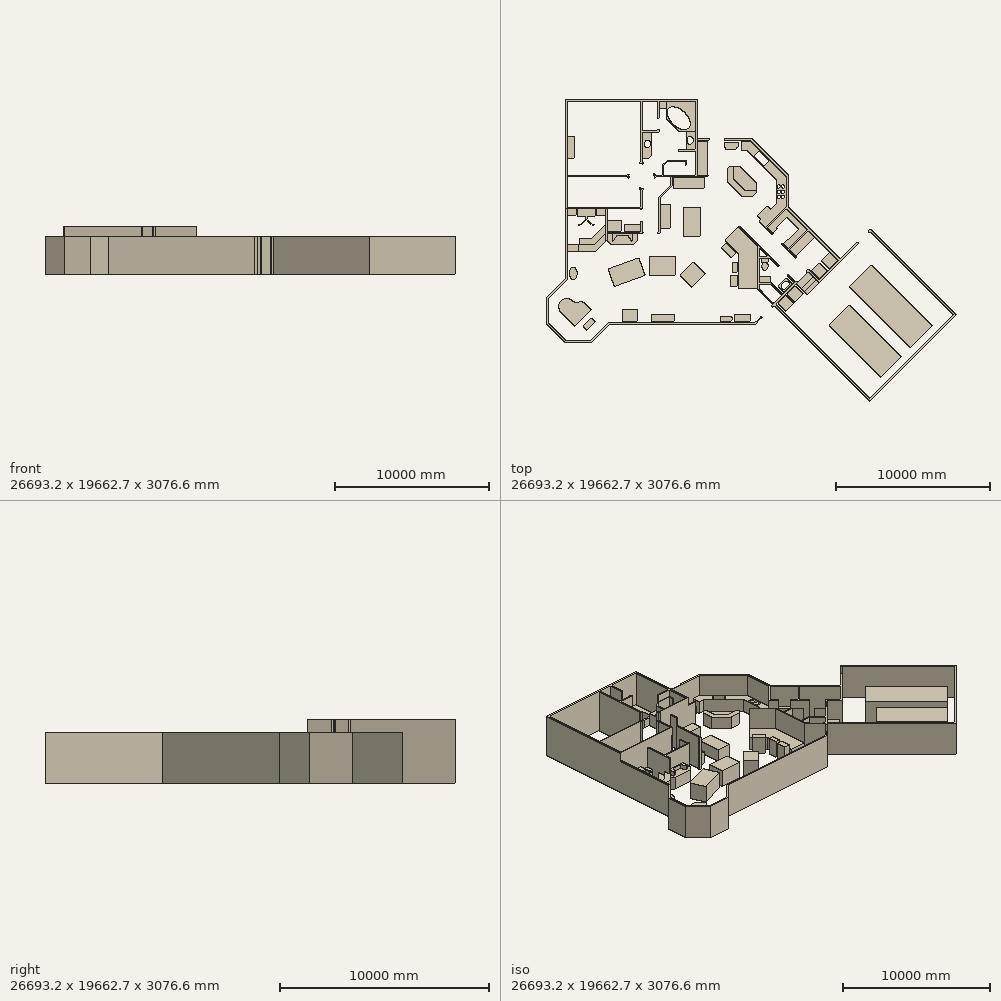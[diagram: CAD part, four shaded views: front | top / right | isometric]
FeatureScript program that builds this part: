
annotation { "Feature Type Name" : "Feature", "Feature Type Description" : "" }
export const myFeature = defineFeature(function(context is Context, id is Id, definition is map)
    precondition{}
    {
        {
            var Q0;
            Q0=qCreatedBy(makeId("Top.planeOp"),FACE);
            var sketch = newSketch(context, id + "F0", { "sketchPlane" : qUnion([Q0])});
            skEllipse(sketch, "E0", {"center": v(0, 0) * mm, "majorRadius": 914.4 * mm, "minorRadius": 533.4 * mm, "majorAxis": v(0.7, -0.7)});
            skLineSegment(sketch, "E1", {"start": v(-646.58, 646.58) * mm, "end": v(646.58, -646.58) * mm, "construction": true});
            skLineSegment(sketch, "E2", {"start": v(377.17, 377.17) * mm, "end": v(-377.17, -377.17) * mm, "construction": true});
            skLineSegment(sketch, "E3", {"start": v(-1281.95, 1090.6) * mm, "end": v(94.8, 1090.6) * mm});
            skLineSegment(sketch, "E4", {"start": v(94.8, 1090.6) * mm, "end": v(1090.6, 94.8) * mm, "construction": true});
            skLineSegment(sketch, "E5", {"start": v(1090.6, 94.8) * mm, "end": v(1090.6, -2043.95) * mm});
            skLineSegment(sketch, "E6", {"start": v(748.55, -368.46) * mm, "end": v(1090.6, -368.46) * mm, "construction": true});
            skLineSegment(sketch, "E7", {"start": v(-368.46, 748.55) * mm, "end": v(-368.46, 1090.6) * mm, "construction": true});
            skLineSegment(sketch, "E8", {"start": v(-368.46, 748.55) * mm, "end": v(436.85, 748.55) * mm, "construction": true});
            skLineSegment(sketch, "E9", {"start": v(748.55, -368.46) * mm, "end": v(748.55, 436.85) * mm, "construction": true});
            skLineSegment(sketch, "E10", {"start": v(377.17, 377.17) * mm, "end": v(592.7, 592.7) * mm, "construction": true});
            skLineSegment(sketch, "E11", {"start": v(-824.75, 1090.6) * mm, "end": v(-824.75, -37.36) * mm});
            skLineSegment(sketch, "E12", {"start": v(-824.75, -37.36) * mm, "end": v(-37.36, -824.75) * mm});
            skLineSegment(sketch, "E13", {"start": v(-37.36, -824.75) * mm, "end": v(1090.6, -824.75) * mm});
            skLineSegment(sketch, "E14", {"start": v(-377.17, -377.17) * mm, "end": v(-431.05, -431.05) * mm, "construction": true});
            skLineSegment(sketch, "E15", {"start": v(368.46, -824.75) * mm, "end": v(368.46, -748.55) * mm, "construction": true});
            skLineSegment(sketch, "E16", {"start": v(368.46, -748.55) * mm, "end": v(1090.6, -748.55) * mm, "construction": true});
            skLineSegment(sketch, "E17", {"start": v(-824.75, 368.46) * mm, "end": v(-748.55, 368.46) * mm, "construction": true});
            skLineSegment(sketch, "E18", {"start": v(-748.55, 368.46) * mm, "end": v(-748.55, 1090.6) * mm, "construction": true});
            skLineSegment(sketch, "E19", {"start": v(-1281.95, 1090.6) * mm, "end": v(-1281.95, 17.6) * mm});
            skLineSegment(sketch, "E20", {"start": v(-1281.95, 17.6) * mm, "end": v(-1370.85, 17.6) * mm});
            skLineSegment(sketch, "E21", {"start": v(-1370.85, 17.6) * mm, "end": v(-1370.85, 1090.6) * mm});
            skLineSegment(sketch, "E22", {"start": v(-1370.85, 1090.6) * mm, "end": v(-2386.85, 1090.6) * mm});
            skLineSegment(sketch, "E23", {"start": v(-2386.85, 1090.6) * mm, "end": v(-2386.85, -820.6) * mm});
            skLineSegment(sketch, "E24", {"start": v(-2386.85, -820.6) * mm, "end": v(-1370.85, -820.6) * mm});
            skLineSegment(sketch, "E25", {"start": v(-1281.95, -909.5) * mm, "end": v(-2386.85, -909.5) * mm});
            skLineSegment(sketch, "E26", {"start": v(-1370.85, -820.6) * mm, "end": v(-1281.95, -820.6) * mm, "construction": true});
            skLineSegment(sketch, "E27", {"start": v(-1777.25, -909.5) * mm, "end": v(-1777.25, -2433.5) * mm});
            skEllipse(sketch, "E28", {"center": v(-2031.25, -1671.5) * mm, "majorRadius": 254 * mm, "minorRadius": 203.2 * mm, "majorAxis": v(0, -1)});
            skLineSegment(sketch, "E29", {"start": v(-2031.25, -1417.5) * mm, "end": v(-2031.25, -1925.5) * mm, "construction": true});
            skLineSegment(sketch, "E30", {"start": v(-2234.45, -1671.5) * mm, "end": v(-1828.05, -1671.5) * mm, "construction": true});
            skLineSegment(sketch, "E31", {"start": v(-1828.05, -1671.5) * mm, "end": v(-1777.25, -1671.5) * mm, "construction": true});
            skLineSegment(sketch, "E32", {"start": v(-1320.05, -820.6) * mm, "end": v(-1320.05, -909.5) * mm, "construction": true});
            skLineSegment(sketch, "E33", {"start": v(-1358.15, -820.6) * mm, "end": v(-1358.15, -909.5) * mm, "construction": true});
            skLineSegment(sketch, "E34", {"start": v(-1396.25, -820.6) * mm, "end": v(-1396.25, -909.5) * mm, "construction": true});
            skLineSegment(sketch, "E35", {"start": v(-1358.15, -858.7) * mm, "end": v(-1320.05, -858.7) * mm, "construction": true});
            skLineSegment(sketch, "E36", {"start": v(-1764.55, -820.6) * mm, "end": v(-1764.55, -909.5) * mm, "construction": true});
            skLineSegment(sketch, "E37", {"start": v(-1802.65, -909.5) * mm, "end": v(-1802.65, -820.6) * mm, "construction": true});
            skLineSegment(sketch, "E38", {"start": v(-1281.95, 633.4) * mm, "end": v(-824.75, 633.4) * mm});
            skLineSegment(sketch, "E39", {"start": v(-1370.85, 1052.5) * mm, "end": v(-1281.95, 1052.5) * mm, "construction": true});
            skLineSegment(sketch, "E40", {"start": v(-1370.85, 1014.4) * mm, "end": v(-1281.95, 1014.4) * mm, "construction": true});
            skLineSegment(sketch, "E41", {"start": v(-1370.85, 1090.6) * mm, "end": v(-1281.95, 1090.6) * mm, "construction": true});
            skLineSegment(sketch, "E42", {"start": v(-2386.85, -909.5) * mm, "end": v(-2386.85, -2827.58) * mm});
            skLineSegment(sketch, "E43", {"start": v(-2386.85, -2827.58) * mm, "end": v(-2279.08, -2935.34) * mm});
            skLineSegment(sketch, "E44", {"start": v(-2279.08, -2935.34) * mm, "end": v(-2341.94, -2998.2) * mm});
            skLineSegment(sketch, "E45", {"start": v(-2341.94, -2998.2) * mm, "end": v(-2449.7, -2890.44) * mm});
            skLineSegment(sketch, "E46", {"start": v(1090.6, -3707.65) * mm, "end": v(-986.98, -3707.65) * mm});
            skLineSegment(sketch, "E47", {"start": v(-1506.78, -3707.65) * mm, "end": v(-1614.54, -3599.88) * mm});
            skLineSegment(sketch, "E48", {"start": v(-1614.54, -3599.88) * mm, "end": v(-1677.4, -3662.74) * mm});
            skLineSegment(sketch, "E49", {"start": v(-1677.4, -3662.74) * mm, "end": v(-1569.64, -3770.5) * mm});
            skLineSegment(sketch, "E50", {"start": v(-1469.96, -3796.55) * mm, "end": v(1230.3, -3796.55) * mm});
            skLineSegment(sketch, "E51", {"start": v(-1777.25, -2433.5) * mm, "end": v(-1929.65, -2585.9) * mm});
            skLineSegment(sketch, "E52", {"start": v(-2386.85, -2585.9) * mm, "end": v(-1929.65, -2585.9) * mm});
            skLineSegment(sketch, "E53", {"start": v(481, -824.75) * mm, "end": v(481, -2043.95) * mm});
            skLineSegment(sketch, "E54", {"start": v(1090.6, -2043.95) * mm, "end": v(-14.3, -2043.95) * mm});
            skLineSegment(sketch, "E55", {"start": v(-14.3, -2043.95) * mm, "end": v(-14.3, -2132.85) * mm});
            skLineSegment(sketch, "E56", {"start": v(-14.3, -2132.85) * mm, "end": v(1090.6, -2132.85) * mm});
            skLineSegment(sketch, "E57.trimOffspring", {"start": v(1090.6, -2132.85) * mm, "end": v(1090.6, -3707.65) * mm});
            skLineSegment(sketch, "E58", {"start": v(-1075.88, -3707.65) * mm, "end": v(-1075.88, -3061.22) * mm});
            skLineSegment(sketch, "E59", {"start": v(-1075.88, -3061.22) * mm, "end": v(-942.08, -2927.42) * mm});
            skLineSegment(sketch, "E60", {"start": v(-942.08, -2927.42) * mm, "end": v(-915.14, -2954.36) * mm});
            skLineSegment(sketch, "E61", {"start": v(-915.14, -2954.36) * mm, "end": v(-703.23, -2742.45) * mm});
            skLineSegment(sketch, "E62", {"start": v(-703.23, -2742.45) * mm, "end": v(481, -2742.45) * mm});
            skLineSegment(sketch, "E63", {"start": v(481, -2742.45) * mm, "end": v(481, -3098.05) * mm});
            skLineSegment(sketch, "E64", {"start": v(481, -3098.05) * mm, "end": v(430.2, -3098.05) * mm});
            skLineSegment(sketch, "E65", {"start": v(430.2, -3098.05) * mm, "end": v(430.2, -2793.25) * mm});
            skLineSegment(sketch, "E66", {"start": v(430.2, -2793.25) * mm, "end": v(-682.18, -2793.25) * mm});
            skLineSegment(sketch, "E67", {"start": v(-682.18, -2793.25) * mm, "end": v(-986.98, -3098.05) * mm});
            skLineSegment(sketch, "E68", {"start": v(-986.98, -3098.05) * mm, "end": v(-986.98, -3707.65) * mm});
            skLineSegment(sketch, "E69.trimOffspring", {"start": v(-1075.88, -3707.65) * mm, "end": v(-1506.78, -3707.65) * mm});
            skLineSegment(sketch, "E70", {"start": v(-1506.78, -3707.65) * mm, "end": v(-1075.88, -3276.75) * mm, "construction": true});
            skLineSegment(sketch, "E71", {"start": v(531.8, -1434.35) * mm, "end": v(938.2, -1434.35) * mm, "construction": true});
            skLineSegment(sketch, "E72", {"start": v(531.8, -1434.35) * mm, "end": v(481, -1434.35) * mm, "construction": true});
            skEllipse(sketch, "E73", {"center": v(735, -1434.35) * mm, "majorRadius": 254 * mm, "minorRadius": 203.2 * mm, "majorAxis": v(0, 1)});
            skLineSegment(sketch, "E74", {"start": v(-2475.75, -2790.76) * mm, "end": v(-2475.75, 1090.6) * mm});
            skLineSegment(sketch, "E75", {"start": v(-2475.75, 1090.6) * mm, "end": v(-6278.2, 1090.6) * mm});
            skLineSegment(sketch, "E76", {"start": v(-6278.2, 1090.6) * mm, "end": v(-7273.99, 94.8) * mm, "construction": true});
            skLineSegment(sketch, "E77", {"start": v(-7273.99, 94.8) * mm, "end": v(-7273.99, -3707.65) * mm});
            skLineSegment(sketch, "E78", {"start": v(-1569.64, -3770.5) * mm, "end": v(-1623.52, -3824.39) * mm});
            skLineSegment(sketch, "E79", {"start": v(-1560.66, -3887.25) * mm, "end": v(-1469.96, -3796.55) * mm});
            skLineSegment(sketch, "E80", {"start": v(-1623.52, -3824.39) * mm, "end": v(-1560.66, -3887.25) * mm});
            skLineSegment(sketch, "E81", {"start": v(-2475.75, -5777.75) * mm, "end": v(-2475.75, -4676.61) * mm});
            skLineSegment(sketch, "E82", {"start": v(-2475.75, -4676.61) * mm, "end": v(-2583.5, -4568.85) * mm});
            skLineSegment(sketch, "E83", {"start": v(-2583.5, -4568.85) * mm, "end": v(-2520.65, -4505.99) * mm});
            skLineSegment(sketch, "E84", {"start": v(-2520.65, -4505.99) * mm, "end": v(-2412.88, -4613.75) * mm});
            skLineSegment(sketch, "E85", {"start": v(-2412.88, -4613.75) * mm, "end": v(-2359, -4559.87) * mm});
            skLineSegment(sketch, "E86", {"start": v(-2359, -4559.87) * mm, "end": v(-2296.14, -4622.73) * mm});
            skLineSegment(sketch, "E87", {"start": v(-2296.14, -4622.73) * mm, "end": v(-2386.85, -4713.43) * mm});
            skLineSegment(sketch, "E88", {"start": v(-2386.85, -4713.43) * mm, "end": v(-2386.85, -5866.65) * mm});
            skLineSegment(sketch, "E89", {"start": v(-7273.99, -3707.65) * mm, "end": v(-3392.63, -3707.65) * mm});
            skLineSegment(sketch, "E90", {"start": v(-3292.95, -3733.68) * mm, "end": v(-3185.19, -3841.45) * mm});
            skLineSegment(sketch, "E91", {"start": v(-3185.19, -3841.45) * mm, "end": v(-3248.05, -3904.3) * mm});
            skLineSegment(sketch, "E92", {"start": v(-3248.05, -3904.3) * mm, "end": v(-3355.81, -3796.55) * mm});
            skLineSegment(sketch, "E93", {"start": v(-3355.81, -3796.55) * mm, "end": v(-7273.99, -3796.55) * mm});
            skLineSegment(sketch, "E94", {"start": v(-3292.95, -3733.68) * mm, "end": v(-3239.07, -3679.8) * mm});
            skLineSegment(sketch, "E95", {"start": v(-3392.63, -3707.65) * mm, "end": v(-3301.93, -3616.94) * mm});
            skLineSegment(sketch, "E96", {"start": v(-3301.93, -3616.94) * mm, "end": v(-3239.07, -3679.8) * mm});
            skLineSegment(sketch, "E97", {"start": v(-2566.45, -2881.46) * mm, "end": v(-2503.59, -2944.32) * mm});
            skLineSegment(sketch, "E98.trimOffspring", {"start": v(-2566.45, -2881.46) * mm, "end": v(-2475.75, -2790.76) * mm});
            skLineSegment(sketch, "E99.trimOffspring", {"start": v(-2503.59, -2944.32) * mm, "end": v(-2449.7, -2890.44) * mm});
            skLineSegment(sketch, "E100", {"start": v(-7273.99, -3796.55) * mm, "end": v(-7273.99, -5777.75) * mm});
            skLineSegment(sketch, "E101", {"start": v(-7273.99, -5777.75) * mm, "end": v(-2475.75, -5777.75) * mm});
            skLineSegment(sketch, "E102.0", {"start": v(-7413.69, 152.66) * mm, "end": v(-7413.69, -5866.65) * mm});
            skLineSegment(sketch, "E102.1", {"start": v(-6336.06, 1230.3) * mm, "end": v(-7413.69, 152.66) * mm, "construction": true});
            skLineSegment(sketch, "E102.2", {"start": v(152.66, 1230.3) * mm, "end": v(-6336.06, 1230.3) * mm});
            skLineSegment(sketch, "E103.0", {"start": v(1230.3, 152.66) * mm, "end": v(1230.3, -3796.55) * mm});
            skLineSegment(sketch, "E104.0", {"start": v(152.66, 1230.3) * mm, "end": v(1230.3, 152.66) * mm, "construction": true});
            skLineSegment(sketch, "E105", {"start": v(-3355.81, -3796.55) * mm, "end": v(-3965.41, -4406.15) * mm, "construction": true});
            skLineSegment(sketch, "E106", {"start": v(-7273.99, -4406.15) * mm, "end": v(-3965.41, -4406.15) * mm, "construction": true});
            skLineSegment(sketch, "E107", {"start": v(-7273.99, -5168.15) * mm, "end": v(-2475.75, -5168.15) * mm, "construction": true});
            skLineSegment(sketch, "E108", {"start": v(-6867.59, -4406.15) * mm, "end": v(-6867.59, -5168.15) * mm, "construction": true});
            skLineSegment(sketch, "E109", {"start": v(-7413.69, -5866.65) * mm, "end": v(-2386.85, -5866.65) * mm});
            skLineSegment(sketch, "E110.bottom", {"start": v(-3034.55, 1090.6) * mm, "end": v(-2475.75, 1090.6) * mm});
            skLineSegment(sketch, "E110.top", {"start": v(-3034.55, 608) * mm, "end": v(-2475.75, 608) * mm});
            skLineSegment(sketch, "E110.left", {"start": v(-3034.55, 1090.6) * mm, "end": v(-3034.55, 608) * mm});
            skLineSegment(sketch, "E110.right", {"start": v(-2475.75, 1090.6) * mm, "end": v(-2475.75, 608) * mm});
            skLineSegment(sketch, "E111.bottom", {"start": v(-3110.75, 1090.6) * mm, "end": v(-4787.15, 1090.6) * mm});
            skLineSegment(sketch, "E111.top", {"start": v(-3110.75, -1347.8) * mm, "end": v(-4787.15, -1347.8) * mm});
            skLineSegment(sketch, "E111.left", {"start": v(-3110.75, 1090.6) * mm, "end": v(-3110.75, -1347.8) * mm});
            skLineSegment(sketch, "E111.right", {"start": v(-4787.15, 1090.6) * mm, "end": v(-4787.15, -1347.8) * mm});
            skLineSegment(sketch, "E112.bottom", {"start": v(-4863.35, 1090.6) * mm, "end": v(-5422.15, 1090.6) * mm});
            skLineSegment(sketch, "E112.top", {"start": v(-4863.35, 608) * mm, "end": v(-5422.15, 608) * mm});
            skLineSegment(sketch, "E112.left", {"start": v(-4863.35, 1090.6) * mm, "end": v(-4863.35, 608) * mm});
            skLineSegment(sketch, "E112.right", {"start": v(-5422.15, 1090.6) * mm, "end": v(-5422.15, 608) * mm});
            skLineSegment(sketch, "E113.trimOffspring", {"start": v(-1281.95, -820.6) * mm, "end": v(-1281.95, -909.5) * mm});
            skLineSegment(sketch, "E114", {"start": v(-1370.85, -820.6) * mm, "end": v(-1370.85, -744.4) * mm});
            skLineSegment(sketch, "E115", {"start": v(-1370.85, -744.4) * mm, "end": v(-1281.95, -744.4) * mm});
            skLineSegment(sketch, "E116", {"start": v(-1281.95, -744.4) * mm, "end": v(-1281.95, -820.6) * mm});
            skLineSegment(sketch, "E117", {"start": v(-1281.95, -820.6) * mm, "end": v(-1281.95, -820.6) * mm});
            skLineSegment(sketch, "E118.bottom", {"start": v(-7273.99, -1167.65) * mm, "end": v(-6791.39, -1167.65) * mm});
            skLineSegment(sketch, "E118.top", {"start": v(-7273.99, -2640.85) * mm, "end": v(-6791.39, -2640.85) * mm});
            skLineSegment(sketch, "E118.left", {"start": v(-7273.99, -1167.65) * mm, "end": v(-7273.99, -2640.85) * mm});
            skLineSegment(sketch, "E118.right", {"start": v(-6791.39, -1167.65) * mm, "end": v(-6791.39, -2640.85) * mm});
            skLineSegment(sketch, "E119.bottom", {"start": v(-7273.99, -3707.65) * mm, "end": v(-6918.39, -3707.65) * mm});
            skLineSegment(sketch, "E119.top", {"start": v(-7273.99, -2945.65) * mm, "end": v(-6918.39, -2945.65) * mm});
            skLineSegment(sketch, "E119.left", {"start": v(-7273.99, -3707.65) * mm, "end": v(-7273.99, -2945.65) * mm});
            skLineSegment(sketch, "E119.right", {"start": v(-6918.39, -3707.65) * mm, "end": v(-6918.39, -2945.65) * mm});
            skLineSegment(sketch, "E120", {"start": v(94.8, 1090.6) * mm, "end": v(1090.6, 1090.6) * mm});
            skLineSegment(sketch, "E121", {"start": v(152.66, 1230.3) * mm, "end": v(1230.3, 1230.3) * mm});
            skLineSegment(sketch, "E122", {"start": v(1090.6, 94.8) * mm, "end": v(1090.6, 1090.6) * mm});
            skLineSegment(sketch, "E123", {"start": v(1230.3, 152.66) * mm, "end": v(1230.3, 1230.3) * mm});
            skLineSegment(sketch, "E124", {"start": v(-6336.06, 1230.3) * mm, "end": v(-7413.69, 1230.3) * mm});
            skLineSegment(sketch, "E125", {"start": v(-6278.2, 1090.6) * mm, "end": v(-7273.99, 1090.6) * mm});
            skLineSegment(sketch, "E126", {"start": v(-7413.69, 152.66) * mm, "end": v(-7413.69, 1230.3) * mm});
            skLineSegment(sketch, "E127", {"start": v(-7273.99, 94.8) * mm, "end": v(-7273.99, 1090.6) * mm});
            skSolve(sketch);
        }
        {
            var Q0;
            {var subQ13=sQuery(id+"F0.wireOp",EDGE,"E20");Q0=makeQuery(id+"F0.imprint","IMPRINT",FACE,{"disambiguationData":[TD([[makeQuery(id+"F0.imprint","IMPRINT",EDGE,{"derivedFrom":subQ13}),-1.0]])]});}
            extrude(context, id + "F1", {"entities" : qUnion([Q0]), "depth" : 3076.57 * mm, "offsetDistance" : 25.4 * mm});
        }
        {
            var Q0;
            {var subQ3=sQuery(id+"F0.wireOp",EDGE,"E53");Q0=makeQuery(id+"F0.imprint","IMPRINT",FACE,{"disambiguationData":[TD([[makeQuery(id+"F0.imprint","IMPRINT",EDGE,{"derivedFrom":subQ3}),1.0]])]});}
            var Q1;
            {var subQ4=sQuery(id+"F0.wireOp",EDGE,"E27");Q1=makeQuery(id+"F0.imprint","IMPRINT",FACE,{"disambiguationData":[TD([[makeQuery(id+"F0.imprint","IMPRINT",EDGE,{"derivedFrom":subQ4}),-1.0]])]});}
            var Q2;
            Q2=makeQuery(id+"F0.imprint","IMPRINT",FACE,{"disambiguationData":[TD([[makeQuery(id+"F0.imprint","IMPRINT",EDGE,{"derivedFrom":sQuery(id+"F0.wireOp",EDGE,"E112.bottom")}),1.0]])]});
            var Q3;
            Q3=makeQuery(id+"F0.imprint","IMPRINT",FACE,{"disambiguationData":[TD([[makeQuery(id+"F0.imprint","IMPRINT",EDGE,{"derivedFrom":sQuery(id+"F0.wireOp",EDGE,"E111.bottom")}),1.0]])]});
            var Q4;
            Q4=makeQuery(id+"F0.imprint","IMPRINT",FACE,{"disambiguationData":[TD([[makeQuery(id+"F0.imprint","IMPRINT",EDGE,{"derivedFrom":sQuery(id+"F0.wireOp",EDGE,"E110.bottom")}),-1.0]])]});
            var Q5;
            Q5=makeQuery(id+"F0.imprint","IMPRINT",FACE,{"disambiguationData":[TD([[makeQuery(id+"F0.imprint","IMPRINT",EDGE,{"derivedFrom":sQuery(id+"F0.wireOp",EDGE,"E118.bottom")}),-1.0]])]});
            var Q6;
            Q6=makeQuery(id+"F0.imprint","IMPRINT",FACE,{"disambiguationData":[TD([[makeQuery(id+"F0.imprint","IMPRINT",EDGE,{"derivedFrom":sQuery(id+"F0.wireOp",EDGE,"E119.bottom")}),1.0]])]});
            var Q7;
            {var subQ5=sQuery(id+"F0.wireOp",EDGE,"E38");Q7=makeQuery(id+"F0.imprint","IMPRINT",FACE,{"disambiguationData":[TD([[makeQuery(id+"F0.imprint","IMPRINT",EDGE,{"derivedFrom":subQ5}),1.0]])]});}
            extrude(context, id + "F2", {"entities" : qUnion([Q0, Q1, Q2, Q3, Q4, Q5, Q6, Q7]), "depth" : 914.4 * mm, "offsetDistance" : 25.4 * mm});
        }
        {
            var Q0;
            Q0=makeQuery(id+"F0.imprint","IMPRINT",FACE,{"disambiguationData":[TD([[makeQuery(id+"F0.imprint","IMPRINT",EDGE,{"derivedFrom":sQuery(id+"F0.wireOp",EDGE,"E0")}),-1.0]])]});
            extrude(context, id + "F3", {"entities" : qUnion([Q0]), "depth" : 609.6 * mm, "offsetDistance" : 25.4 * mm});
        }
        {
            var Q0;
            Q0=qCreatedBy(makeId("Top.planeOp"),FACE);
            var sketch = newSketch(context, id + "F4", { "sketchPlane" : qUnion([Q0])});
            skLineSegment(sketch, "E128", {"start": v(-7413.69, -5866.65) * mm, "end": v(-7413.69, -10507.78) * mm});
            skLineSegment(sketch, "E129", {"start": v(-7413.69, -10507.78) * mm, "end": v(-8618.88, -11712.98) * mm});
            skLineSegment(sketch, "E130", {"start": v(-8618.88, -11712.98) * mm, "end": v(-8618.88, -13417.38) * mm});
            skLineSegment(sketch, "E131", {"start": v(-8618.88, -13417.38) * mm, "end": v(-7413.69, -14622.58) * mm});
            skLineSegment(sketch, "E132", {"start": v(-7413.69, -14622.58) * mm, "end": v(-5709.28, -14622.58) * mm});
            skLineSegment(sketch, "E133", {"start": v(-5709.28, -14622.58) * mm, "end": v(-4504.08, -13417.38) * mm});
            skLineSegment(sketch, "E134", {"start": v(-4504.08, -13417.38) * mm, "end": v(5003.07, -13417.38) * mm});
            skLineSegment(sketch, "E135", {"start": v(-7413.69, -5866.65) * mm, "end": v(-7273.99, -5866.65) * mm});
            skLineSegment(sketch, "E136", {"start": v(-7273.99, -5866.65) * mm, "end": v(-7273.99, -10565.65) * mm});
            skLineSegment(sketch, "E137", {"start": v(-7273.99, -10565.65) * mm, "end": v(-8479.18, -11770.84) * mm});
            skLineSegment(sketch, "E138", {"start": v(-4759.39, -7873.25) * mm, "end": v(-4759.39, -5866.65) * mm});
            skLineSegment(sketch, "E139", {"start": v(-4759.39, -5866.65) * mm, "end": v(-4670.49, -5866.65) * mm});
            skLineSegment(sketch, "E140", {"start": v(-4670.49, -5866.65) * mm, "end": v(-4670.49, -7416.05) * mm});
            skLineSegment(sketch, "E141.0", {"start": v(-4561.95, -13277.68) * mm, "end": v(4945.2, -13277.68) * mm});
            skLineSegment(sketch, "E141.1", {"start": v(-8479.18, -11770.84) * mm, "end": v(-8479.18, -13359.52) * mm});
            skLineSegment(sketch, "E141.2", {"start": v(-8479.18, -13359.52) * mm, "end": v(-7355.82, -14482.88) * mm});
            skLineSegment(sketch, "E141.3", {"start": v(-7355.82, -14482.88) * mm, "end": v(-5767.15, -14482.88) * mm});
            skLineSegment(sketch, "E141.4", {"start": v(-5767.15, -14482.88) * mm, "end": v(-4561.95, -13277.68) * mm});
            skLineSegment(sketch, "E142.bottom", {"start": v(-4614.6, -9813.74) * mm, "end": v(-2609.68, -9084.01) * mm});
            skLineSegment(sketch, "E142.top", {"start": v(-4197.61, -10959.42) * mm, "end": v(-2192.68, -10229.68) * mm});
            skLineSegment(sketch, "E142.left", {"start": v(-4614.6, -9813.74) * mm, "end": v(-4197.61, -10959.42) * mm});
            skLineSegment(sketch, "E142.right", {"start": v(-2609.68, -9084.01) * mm, "end": v(-2192.68, -10229.68) * mm});
            skLineSegment(sketch, "E143.bottom", {"start": v(-1887.88, -9010.48) * mm, "end": v(-211.48, -9010.48) * mm});
            skLineSegment(sketch, "E143.top", {"start": v(-1887.88, -10229.68) * mm, "end": v(-211.48, -10229.68) * mm});
            skLineSegment(sketch, "E143.left", {"start": v(-1887.88, -9010.48) * mm, "end": v(-1887.88, -10229.68) * mm});
            skLineSegment(sketch, "E143.right", {"start": v(-211.48, -9010.48) * mm, "end": v(-211.48, -10229.68) * mm});
            skLineSegment(sketch, "E144.bottom", {"start": v(955.42, -9367.58) * mm, "end": v(1709.76, -10121.92) * mm});
            skLineSegment(sketch, "E144.top", {"start": v(93.32, -10229.68) * mm, "end": v(847.66, -10984.03) * mm});
            skLineSegment(sketch, "E144.left", {"start": v(955.42, -9367.58) * mm, "end": v(93.32, -10229.68) * mm});
            skLineSegment(sketch, "E144.right", {"start": v(1709.76, -10121.92) * mm, "end": v(847.66, -10984.03) * mm});
            skLineSegment(sketch, "E145", {"start": v(-4097.68, -13277.68) * mm, "end": v(-4097.68, -13417.38) * mm, "construction": true});
            skLineSegment(sketch, "E146", {"start": v(-2268.88, -13277.68) * mm, "end": v(-2268.88, -13417.38) * mm, "construction": true});
            skLineSegment(sketch, "E147", {"start": v(169.52, -13277.68) * mm, "end": v(169.52, -13417.38) * mm, "construction": true});
            skLineSegment(sketch, "E148", {"start": v(1998.32, -13277.68) * mm, "end": v(1998.32, -13417.38) * mm, "construction": true});
            skLineSegment(sketch, "E149", {"start": v(-2268.88, -13277.68) * mm, "end": v(-1887.88, -10229.68) * mm, "construction": true});
            skLineSegment(sketch, "E150", {"start": v(169.52, -13277.68) * mm, "end": v(-211.48, -10229.68) * mm, "construction": true});
            skLineSegment(sketch, "E151", {"start": v(3870.2, -11101.89) * mm, "end": v(5140.2, -11101.89) * mm});
            skLineSegment(sketch, "E152", {"start": v(5140.2, -11101.89) * mm, "end": v(5140.2, -8307.89) * mm});
            skLineSegment(sketch, "E153", {"start": v(5140.2, -8307.89) * mm, "end": v(3896.43, -7064.12) * mm});
            skLineSegment(sketch, "E154", {"start": v(3896.43, -7064.12) * mm, "end": v(2998.4, -7962.15) * mm});
            skLineSegment(sketch, "E155", {"start": v(2998.4, -7962.15) * mm, "end": v(3870.2, -8833.94) * mm});
            skLineSegment(sketch, "E156", {"start": v(3870.2, -8833.94) * mm, "end": v(3870.2, -11101.89) * mm});
            skCircle(sketch, "E157", {"center": v(2955.8, -9212.7) * mm, "radius": 914.4 * mm, "construction": true});
            skLineSegment(sketch, "E158", {"start": v(6130.6, -12092.29) * mm, "end": v(6022.84, -12200.05) * mm});
            skLineSegment(sketch, "E159", {"start": v(5003.07, -13417.38) * mm, "end": v(5151.75, -13268.7) * mm});
            skLineSegment(sketch, "E160", {"start": v(5052.97, -13169.92) * mm, "end": v(5084.4, -13201.35) * mm});
            skLineSegment(sketch, "E161", {"start": v(5084.4, -13201.35) * mm, "end": v(5335.85, -12949.9) * mm});
            skLineSegment(sketch, "E162", {"start": v(5335.85, -12949.9) * mm, "end": v(5304.42, -12918.47) * mm});
            skLineSegment(sketch, "E163", {"start": v(5151.75, -13268.7) * mm, "end": v(5120.32, -13237.27) * mm});
            skLineSegment(sketch, "E164", {"start": v(5120.32, -13237.27) * mm, "end": v(5371.77, -12985.83) * mm});
            skLineSegment(sketch, "E165", {"start": v(5371.77, -12985.83) * mm, "end": v(5403.2, -13017.26) * mm});
            skLineSegment(sketch, "E166.trimOffspring", {"start": v(5052.97, -13169.92) * mm, "end": v(4945.2, -13277.68) * mm});
            skLineSegment(sketch, "E167.trimOffspring", {"start": v(5403.2, -13017.26) * mm, "end": v(5439.12, -12981.34) * mm});
            skLineSegment(sketch, "E168", {"start": v(5340.34, -12882.55) * mm, "end": v(5353.8, -12896.02) * mm});
            skLineSegment(sketch, "E169", {"start": v(6022.84, -12200.05) * mm, "end": v(6036.3, -12213.52) * mm});
            skLineSegment(sketch, "E170.trimOffspring", {"start": v(5340.34, -12882.55) * mm, "end": v(5304.42, -12918.47) * mm});
            skLineSegment(sketch, "E171.trimOffspring", {"start": v(6121.62, -12298.84) * mm, "end": v(6858, -11562.45) * mm});
            skArc(sketch, "E172", {"start": v(5340.34, -12882.55) * mm, "mid": v(5060.67, -12123.61) * mm, "end": v(5456.66, -11418.35) * mm, "construction": true});
            skLineSegment(sketch, "E173", {"start": v(-7273.99, -10565.65) * mm, "end": v(-4670.49, -7962.15) * mm, "construction": true});
            skLineSegment(sketch, "E174", {"start": v(-6746.57, -13558.49) * mm, "end": v(-5668.94, -12480.86) * mm});
            skLineSegment(sketch, "E175", {"start": v(-5668.94, -12480.86) * mm, "end": v(-6100, -12049.8) * mm});
            skLineSegment(sketch, "E176", {"start": v(-6746.57, -13558.49) * mm, "end": v(-7662.56, -12642.5) * mm});
            skArc(sketch, "E177", {"start": v(-6100, -12049.8) * mm, "mid": v(-6289.81, -11948.22) * mm, "end": v(-6504.1, -11968.98) * mm});
            skArc(sketch, "E178", {"start": v(-6504.1, -11968.98) * mm, "mid": v(-6718.4, -11989.75) * mm, "end": v(-6908.21, -11888.16) * mm});
            skArc(sketch, "E179", {"start": v(-6908.21, -11888.16) * mm, "mid": v(-7662.56, -11888.16) * mm, "end": v(-7662.56, -12642.5) * mm});
            skLineSegment(sketch, "E180", {"start": v(-7662.56, -12642.5) * mm, "end": v(-6908.21, -11888.16) * mm, "construction": true});
            skLineSegment(sketch, "E181.bottom", {"start": v(-5974.27, -13791.97) * mm, "end": v(-5435.45, -13253.16) * mm});
            skLineSegment(sketch, "E181.top", {"start": v(-6225.71, -13540.53) * mm, "end": v(-5686.9, -13001.71) * mm});
            skLineSegment(sketch, "E181.left", {"start": v(-5974.27, -13791.97) * mm, "end": v(-6225.71, -13540.53) * mm});
            skLineSegment(sketch, "E181.right", {"start": v(-5435.45, -13253.16) * mm, "end": v(-5686.9, -13001.71) * mm});
            skLineSegment(sketch, "E182", {"start": v(-6207.75, -13019.67) * mm, "end": v(-5956.3, -13271.12) * mm, "construction": true});
            skLineSegment(sketch, "E183", {"start": v(-6561.48, -14482.88) * mm, "end": v(-6561.48, -14622.58) * mm, "construction": true});
            skLineSegment(sketch, "E184", {"start": v(-5951.88, -14482.88) * mm, "end": v(-5951.88, -14622.58) * mm, "construction": true});
            skLineSegment(sketch, "E185", {"start": v(-7171.08, -14482.88) * mm, "end": v(-7171.08, -14622.58) * mm, "construction": true});
            skLineSegment(sketch, "E186", {"start": v(-5662.56, -14378.3) * mm, "end": v(-5563.78, -14477.08) * mm, "construction": true});
            skLineSegment(sketch, "E187", {"start": v(-4800.46, -13516.2) * mm, "end": v(-4701.68, -13614.97) * mm, "construction": true});
            skLineSegment(sketch, "E188.bottom", {"start": v(-3567.95, -6501.65) * mm, "end": v(-2501.15, -6501.65) * mm});
            skLineSegment(sketch, "E188.top", {"start": v(-3542.55, -6527.05) * mm, "end": v(-2526.55, -6527.05) * mm});
            skLineSegment(sketch, "E188.left", {"start": v(-3567.95, -6501.65) * mm, "end": v(-3567.95, -6527.05) * mm});
            skLineSegment(sketch, "E188.right", {"start": v(-2501.15, -6501.65) * mm, "end": v(-2501.15, -6527.05) * mm});
            skLineSegment(sketch, "E189.bottom", {"start": v(-4645.09, -7390.65) * mm, "end": v(-3756.09, -7390.65) * mm});
            skLineSegment(sketch, "E189.top", {"start": v(-4645.09, -6628.65) * mm, "end": v(-3756.09, -6628.65) * mm});
            skLineSegment(sketch, "E189.left", {"start": v(-4645.09, -7390.65) * mm, "end": v(-4645.09, -6628.65) * mm});
            skLineSegment(sketch, "E189.right", {"start": v(-3756.09, -7390.65) * mm, "end": v(-3756.09, -6628.65) * mm});
            skLineSegment(sketch, "E190.bottom", {"start": v(-3691.28, -12464.88) * mm, "end": v(-2675.28, -12464.88) * mm});
            skLineSegment(sketch, "E190.top", {"start": v(-3691.28, -13226.88) * mm, "end": v(-2675.28, -13226.88) * mm});
            skLineSegment(sketch, "E190.left", {"start": v(-3691.28, -12464.88) * mm, "end": v(-3691.28, -13226.88) * mm});
            skLineSegment(sketch, "E190.right", {"start": v(-2675.28, -12464.88) * mm, "end": v(-2675.28, -13226.88) * mm});
            skLineSegment(sketch, "E191.bottom", {"start": v(4640.4, -13252.28) * mm, "end": v(3624.4, -13252.28) * mm});
            skLineSegment(sketch, "E191.top", {"start": v(4640.4, -12744.28) * mm, "end": v(3624.4, -12744.28) * mm});
            skLineSegment(sketch, "E191.left", {"start": v(4640.4, -13252.28) * mm, "end": v(4640.4, -12744.28) * mm});
            skLineSegment(sketch, "E191.right", {"start": v(3624.4, -13252.28) * mm, "end": v(3624.4, -12744.28) * mm});
            skLineSegment(sketch, "E192", {"start": v(3281.5, -12871.28) * mm, "end": v(2684.6, -12871.28) * mm});
            skLineSegment(sketch, "E193", {"start": v(2684.6, -12871.28) * mm, "end": v(2684.6, -13252.28) * mm});
            skLineSegment(sketch, "E194", {"start": v(2684.6, -13252.28) * mm, "end": v(3281.5, -13252.28) * mm});
            skArc(sketch, "E195", {"start": v(3281.5, -13252.28) * mm, "mid": v(3472, -13061.78) * mm, "end": v(3281.5, -12871.28) * mm});
            skLineSegment(sketch, "E196.bottom", {"start": v(3387.6, -10949.49) * mm, "end": v(3844.8, -10949.49) * mm});
            skLineSegment(sketch, "E196.top", {"start": v(3387.6, -10212.89) * mm, "end": v(3844.8, -10212.89) * mm});
            skLineSegment(sketch, "E196.left", {"start": v(3387.6, -10949.49) * mm, "end": v(3387.6, -10212.89) * mm});
            skLineSegment(sketch, "E196.right", {"start": v(3844.8, -10949.49) * mm, "end": v(3844.8, -10212.89) * mm});
            skLineSegment(sketch, "E197.bottom", {"start": v(3514.6, -10009.69) * mm, "end": v(3844.8, -10009.69) * mm});
            skLineSegment(sketch, "E197.top", {"start": v(3514.6, -9374.69) * mm, "end": v(3844.8, -9374.69) * mm});
            skLineSegment(sketch, "E197.left", {"start": v(3514.6, -10009.69) * mm, "end": v(3514.6, -9374.69) * mm});
            skLineSegment(sketch, "E197.right", {"start": v(3844.8, -10009.69) * mm, "end": v(3844.8, -9374.69) * mm});
            skLineSegment(sketch, "E198.bottom", {"start": v(2774.6, -8456.77) * mm, "end": v(3403.22, -9085.38) * mm});
            skLineSegment(sketch, "E198.top", {"start": v(3115.86, -8115.52) * mm, "end": v(3744.47, -8744.13) * mm});
            skLineSegment(sketch, "E198.left", {"start": v(2774.6, -8456.77) * mm, "end": v(3115.86, -8115.52) * mm});
            skLineSegment(sketch, "E198.right", {"start": v(3403.22, -9085.38) * mm, "end": v(3744.47, -8744.13) * mm});
            skEllipse(sketch, "E199", {"center": v(-6873.14, -10102.07) * mm, "majorRadius": 406.4 * mm, "minorRadius": 254 * mm, "majorAxis": v(0, -1)});
            skLineSegment(sketch, "E200.bottom", {"start": v(-1811.68, -13226.88) * mm, "end": v(-287.68, -13226.88) * mm});
            skLineSegment(sketch, "E200.top", {"start": v(-1811.68, -12769.68) * mm, "end": v(-287.68, -12769.68) * mm});
            skLineSegment(sketch, "E200.left", {"start": v(-1811.68, -13226.88) * mm, "end": v(-1811.68, -12769.68) * mm});
            skLineSegment(sketch, "E200.right", {"start": v(-287.68, -13226.88) * mm, "end": v(-287.68, -12769.68) * mm});
            skLineSegment(sketch, "E201", {"start": v(-2268.88, -13277.68) * mm, "end": v(-1811.68, -13226.88) * mm, "construction": true});
            skLineSegment(sketch, "E202", {"start": v(-287.68, -13226.88) * mm, "end": v(169.52, -13277.68) * mm, "construction": true});
            skLineSegment(sketch, "E203.bottom", {"start": v(-6626.29, -5892.05) * mm, "end": v(-5407.09, -5892.05) * mm});
            skLineSegment(sketch, "E203.top", {"start": v(-6626.29, -6374.65) * mm, "end": v(-6588.19, -6374.65) * mm, "construction": true});
            skLineSegment(sketch, "E203.left", {"start": v(-6626.29, -5892.05) * mm, "end": v(-6626.29, -6374.65) * mm});
            skLineSegment(sketch, "E203.right", {"start": v(-5407.09, -5892.05) * mm, "end": v(-5407.09, -6374.65) * mm});
            skArc(sketch, "E204", {"start": v(-6016.69, -6374.65) * mm, "mid": v(-6195.24, -6805.7) * mm, "end": v(-6626.29, -6984.25) * mm});
            skArc(sketch, "E205", {"start": v(-6016.69, -6374.65) * mm, "mid": v(-5838.14, -6805.7) * mm, "end": v(-5407.09, -6984.25) * mm});
            skLineSegment(sketch, "E206", {"start": v(-6626.29, -6374.65) * mm, "end": v(-6626.29, -6984.25) * mm});
            skLineSegment(sketch, "E207", {"start": v(-5407.09, -6374.65) * mm, "end": v(-5407.09, -6984.25) * mm});
            skLineSegment(sketch, "E208.0", {"start": v(-6588.19, -6374.65) * mm, "end": v(-6588.19, -6944.87) * mm});
            skArc(sketch, "E208.1", {"start": v(-6054.79, -6374.65) * mm, "mid": v(-6208.92, -6765.06) * mm, "end": v(-6588.19, -6944.87) * mm});
            skLineSegment(sketch, "E209.0", {"start": v(-5445.19, -6374.65) * mm, "end": v(-5445.19, -6944.87) * mm});
            skArc(sketch, "E209.1", {"start": v(-5978.59, -6374.65) * mm, "mid": v(-5824.45, -6765.06) * mm, "end": v(-5445.19, -6944.87) * mm});
            skLineSegment(sketch, "E210.trimOffspring", {"start": v(-6054.79, -6374.65) * mm, "end": v(-5978.59, -6374.65) * mm, "construction": true});
            skLineSegment(sketch, "E211.trimOffspring", {"start": v(-5445.19, -6374.65) * mm, "end": v(-5407.09, -6374.65) * mm, "construction": true});
            skLineSegment(sketch, "E212", {"start": v(-6588.19, -6374.65) * mm, "end": v(-6054.79, -6374.65) * mm});
            skLineSegment(sketch, "E213", {"start": v(-5978.59, -6374.65) * mm, "end": v(-5445.19, -6374.65) * mm});
            skLineSegment(sketch, "E214", {"start": v(5140.2, -11101.89) * mm, "end": v(6130.6, -12092.29) * mm});
            skLineSegment(sketch, "E215", {"start": v(5353.8, -12896.02) * mm, "end": v(6036.3, -12213.52) * mm});
            skLineSegment(sketch, "E216", {"start": v(5358.3, -12900.51) * mm, "end": v(6040.8, -12218.01) * mm});
            skLineSegment(sketch, "E217.trimOffspring", {"start": v(5358.3, -12900.51) * mm, "end": v(5439.12, -12981.34) * mm});
            skLineSegment(sketch, "E218.trimOffspring", {"start": v(6040.8, -12218.01) * mm, "end": v(6121.62, -12298.84) * mm});
            skLineSegment(sketch, "E219", {"start": v(6193.46, -12029.43) * mm, "end": v(6139.58, -11975.55) * mm});
            skLineSegment(sketch, "E220", {"start": v(5229.1, -11065.06) * mm, "end": v(5229.1, -10784.45) * mm});
            skLineSegment(sketch, "E221", {"start": v(5229.1, -8271.06) * mm, "end": v(3959.3, -7001.26) * mm});
            skLineSegment(sketch, "E222", {"start": v(3959.3, -7001.26) * mm, "end": v(3896.43, -7064.12) * mm});
            skLineSegment(sketch, "E223", {"start": v(5457.08, -11293.05) * mm, "end": v(5398.7, -11351.42) * mm});
            skLineSegment(sketch, "E224", {"start": v(5398.7, -11351.42) * mm, "end": v(6081.2, -12033.92) * mm});
            skLineSegment(sketch, "E225", {"start": v(6081.2, -12033.92) * mm, "end": v(6139.58, -11975.55) * mm});
            skLineSegment(sketch, "E226.trimOffspring", {"start": v(5457.08, -11293.05) * mm, "end": v(5229.1, -11065.06) * mm});
            skLineSegment(sketch, "E227", {"start": v(5954.27, -10784.45) * mm, "end": v(6696.36, -11526.53) * mm});
            skLineSegment(sketch, "E228", {"start": v(5991.1, -10695.55) * mm, "end": v(6858, -11562.45) * mm});
            skLineSegment(sketch, "E229.trimOffspring", {"start": v(5229.1, -10695.55) * mm, "end": v(5229.1, -8271.06) * mm});
            skLineSegment(sketch, "E230", {"start": v(6193.46, -12029.43) * mm, "end": v(6696.36, -11526.53) * mm});
            skLineSegment(sketch, "E231", {"start": v(5229.1, -10784.45) * mm, "end": v(5954.27, -10784.45) * mm});
            skLineSegment(sketch, "E232", {"start": v(5229.1, -10695.55) * mm, "end": v(5991.1, -10695.55) * mm});
            skLineSegment(sketch, "E233", {"start": v(-3567.95, -6527.05) * mm, "end": v(-3567.95, -7390.65) * mm});
            skLineSegment(sketch, "E234", {"start": v(-3567.95, -7390.65) * mm, "end": v(-2501.15, -7390.65) * mm});
            skLineSegment(sketch, "E235", {"start": v(-2501.15, -7390.65) * mm, "end": v(-2501.15, -6527.05) * mm});
            skLineSegment(sketch, "E236", {"start": v(-3542.55, -6527.05) * mm, "end": v(-3542.55, -6908.05) * mm});
            skLineSegment(sketch, "E237", {"start": v(-3542.55, -6908.05) * mm, "end": v(-2526.55, -6908.05) * mm});
            skLineSegment(sketch, "E238", {"start": v(-2526.55, -6908.05) * mm, "end": v(-2526.55, -6527.05) * mm});
            skLineSegment(sketch, "E239", {"start": v(-7273.99, -6336.55) * mm, "end": v(-6651.69, -6336.55) * mm});
            skLineSegment(sketch, "E240", {"start": v(-4759.39, -7962.15) * mm, "end": v(-4670.49, -7962.15) * mm});
            skLineSegment(sketch, "E241", {"start": v(-7273.99, -5866.65) * mm, "end": v(-6651.69, -5866.65) * mm});
            skLineSegment(sketch, "E242", {"start": v(-6651.69, -5866.65) * mm, "end": v(-6651.69, -6336.55) * mm});
            skLineSegment(sketch, "E243", {"start": v(-4759.39, -5866.65) * mm, "end": v(-5381.69, -5866.65) * mm});
            skLineSegment(sketch, "E244", {"start": v(-5381.69, -5866.65) * mm, "end": v(-5381.69, -6336.55) * mm});
            skLineSegment(sketch, "E245.trimOffspring", {"start": v(-5381.69, -6336.55) * mm, "end": v(-4759.39, -6336.55) * mm});
            skLineSegment(sketch, "E246", {"start": v(-2475.75, -7416.05) * mm, "end": v(-2475.75, -6704.85) * mm});
            skLineSegment(sketch, "E247", {"start": v(-2475.75, -6704.85) * mm, "end": v(-2386.85, -6704.85) * mm});
            skLineSegment(sketch, "E248", {"start": v(-2386.85, -6704.85) * mm, "end": v(-2386.85, -7504.95) * mm});
            skLineSegment(sketch, "E249", {"start": v(-4670.49, -7962.15) * mm, "end": v(-4670.49, -7962.15) * mm});
            skLineSegment(sketch, "E250.bottom", {"start": v(-2475.75, -5866.65) * mm, "end": v(-2386.85, -5866.65) * mm});
            skLineSegment(sketch, "E250.top", {"start": v(-2475.75, -5942.85) * mm, "end": v(-2386.85, -5942.85) * mm});
            skLineSegment(sketch, "E250.left", {"start": v(-2386.85, -5866.65) * mm, "end": v(-2386.85, -5942.85) * mm});
            skLineSegment(sketch, "E250.right", {"start": v(-2475.75, -5866.65) * mm, "end": v(-2475.75, -5942.85) * mm});
            skLineSegment(sketch, "E251", {"start": v(-4759.39, -7476.3) * mm, "end": v(-5525, -8241.92) * mm});
            skLineSegment(sketch, "E252", {"start": v(-4750.86, -8042.52) * mm, "end": v(-4670.49, -7962.15) * mm});
            skLineSegment(sketch, "E253", {"start": v(-4750.86, -8042.52) * mm, "end": v(-5253.75, -8545.41) * mm});
            skLineSegment(sketch, "E254", {"start": v(-5525, -8241.92) * mm, "end": v(-7273.99, -8241.92) * mm});
            skLineSegment(sketch, "E255", {"start": v(-5253.75, -8545.41) * mm, "end": v(-5356.66, -8648.32) * mm});
            skLineSegment(sketch, "E256", {"start": v(-5356.66, -8648.32) * mm, "end": v(-7273.99, -8648.32) * mm});
            skLineSegment(sketch, "E257", {"start": v(-4670.49, -7873.25) * mm, "end": v(-4759.39, -7873.25) * mm});
            skLineSegment(sketch, "E258", {"start": v(-4759.39, -7962.15) * mm, "end": v(-4759.39, -7873.25) * mm});
            skLineSegment(sketch, "E259", {"start": v(-4670.49, -7416.05) * mm, "end": v(-2475.75, -7416.05) * mm});
            skLineSegment(sketch, "E260", {"start": v(-4670.49, -7504.95) * mm, "end": v(-2386.85, -7504.95) * mm});
            skLineSegment(sketch, "E261.trimOffspring", {"start": v(-4670.49, -7504.95) * mm, "end": v(-4670.49, -7962.15) * mm});
            skLineSegment(sketch, "E262", {"start": v(-7223.19, -8241.92) * mm, "end": v(-7223.19, -8648.32) * mm});
            skLineSegment(sketch, "E263", {"start": v(-6511.99, -8241.92) * mm, "end": v(-6511.99, -8648.32) * mm});
            skLineSegment(sketch, "E264", {"start": v(-6461.19, -8241.92) * mm, "end": v(-6461.19, -7835.52) * mm});
            skLineSegment(sketch, "E265", {"start": v(-6461.19, -7835.52) * mm, "end": v(-5693.33, -7835.52) * mm});
            skLineSegment(sketch, "E266", {"start": v(-5693.33, -7835.52) * mm, "end": v(-4759.39, -6901.57) * mm});
            skLineSegment(sketch, "E267", {"start": v(-4759.39, -7476.3) * mm, "end": v(-5046.76, -7188.94) * mm, "construction": true});
            skLineSegment(sketch, "E268", {"start": v(-5693.33, -7835.52) * mm, "end": v(-5046.76, -7188.94) * mm, "construction": true});
            skLineSegment(sketch, "E269", {"start": v(-4345.02, -7504.95) * mm, "end": v(-4345.02, -8000.25) * mm});
            skLineSegment(sketch, "E270", {"start": v(-4345.02, -8000.25) * mm, "end": v(-4243.42, -8000.25) * mm});
            skLineSegment(sketch, "E271", {"start": v(-4243.42, -8000.25) * mm, "end": v(-4027.52, -7606.55) * mm});
            skLineSegment(sketch, "E272", {"start": v(-4027.52, -7606.55) * mm, "end": v(-3316.32, -7606.55) * mm});
            skLineSegment(sketch, "E273", {"start": v(-3316.32, -7606.55) * mm, "end": v(-3100.42, -8000.25) * mm});
            skLineSegment(sketch, "E274", {"start": v(-3100.42, -8000.25) * mm, "end": v(-2998.82, -8000.25) * mm});
            skLineSegment(sketch, "E275", {"start": v(-2998.82, -8000.25) * mm, "end": v(-2998.82, -7504.95) * mm});
            skLineSegment(sketch, "E276", {"start": v(-4670.49, -7962.15) * mm, "end": v(-4429.19, -8203.45) * mm});
            skLineSegment(sketch, "E277", {"start": v(-4429.19, -8203.45) * mm, "end": v(-2914.65, -8203.45) * mm});
            skLineSegment(sketch, "E278", {"start": v(-2914.65, -8203.45) * mm, "end": v(-2673.35, -7962.15) * mm});
            skLineSegment(sketch, "E279", {"start": v(-2673.35, -7962.15) * mm, "end": v(-2673.35, -7504.95) * mm});
            skSolve(sketch);
        }
        {
            var Q0;
            Q0=makeQuery(id+"F4.imprint","IMPRINT",FACE,{"disambiguationData":[TD([[makeQuery(id+"F4.imprint","IMPRINT",EDGE,{"derivedFrom":sQuery(id+"F4.wireOp",EDGE,"E128")}),1.0]])]});
            var Q1;
            {var subQ0=sQuery(id+"F4.wireOp",EDGE,"tu0bnIMI-XPDQ-O63l-zV0n-bsMbi5vPYYDK");Q1=makeQuery(id+"F4.imprint","IMPRINT",FACE,{"disambiguationData":[TD([[makeQuery(id+"F4.imprint","IMPRINT",EDGE,{"derivedFrom":subQ0}),1.0]])]});}
            var Q2;
            Q2=makeQuery(id+"F4.imprint","IMPRINT",FACE,{"disambiguationData":[TD([[makeQuery(id+"F4.imprint","IMPRINT",EDGE,{"derivedFrom":sQuery(id+"F4.wireOp",EDGE,"cVDFVvJU-CdxU-lq4t-xSE6-bGD4vrnjslK9")}),-1.0]])]});
            var Q3;
            {var subQ0=sQuery(id+"F4.wireOp",EDGE,"E139");Q3=makeQuery(id+"F4.imprint","IMPRINT",FACE,{"disambiguationData":[TD([[makeQuery(id+"F4.imprint","IMPRINT",EDGE,{"derivedFrom":subQ0}),-1.0]])]});}
            var Q4;
            {var subQ0=sQuery(id+"F4.wireOp",EDGE,"zE60XHoQ-awIa-BXBa-y9rd-91rddcirCjtx");Q4=makeQuery(id+"F4.imprint","IMPRINT",FACE,{"disambiguationData":[TD([[makeQuery(id+"F4.imprint","IMPRINT",EDGE,{"derivedFrom":subQ0}),-1.0]])]});}
            var Q5;
            Q5=makeQuery(id+"F4.imprint","IMPRINT",FACE,{"disambiguationData":[TD([[makeQuery(id+"F4.imprint","IMPRINT",EDGE,{"derivedFrom":sQuery(id+"F4.wireOp",EDGE,"E250.bottom")}),-1.0]])]});
            var Q6;
            {var subQ0=sQuery(id+"F4.wireOp",EDGE,"E240");Q6=makeQuery(id+"F4.imprint","IMPRINT",FACE,{"disambiguationData":[TD([[makeQuery(id+"F4.imprint","IMPRINT",EDGE,{"derivedFrom":subQ0}),1.0]])]});}
            extrude(context, id + "F5", {"entities" : qUnion([Q0, Q1, Q2, Q3, Q4, Q5, Q6]), "operationType" : NewBodyOperationType.ADD, "depth" : 2466.97 * mm, "offsetDistance" : 25.4 * mm});
        }
        {
            var Q0;
            {var subQ0=sQuery(id+"F4.wireOp",EDGE,"t8M4w7Kw-P3rl-P2br-wT64-1wpeZmyCxikI");Q0=makeQuery(id+"F4.imprint","IMPRINT",FACE,{"disambiguationData":[TD([[makeQuery(id+"F4.imprint","IMPRINT",EDGE,{"derivedFrom":subQ0}),1.0]])]});}
            var Q1;
            Q1=makeQuery(id+"F4.imprint","IMPRINT",FACE,{"disambiguationData":[TD([[makeQuery(id+"F4.imprint","IMPRINT",EDGE,{"derivedFrom":sQuery(id+"F4.wireOp",EDGE,"E142.bottom")}),-1.0]])]});
            var Q2;
            Q2=makeQuery(id+"F4.imprint","IMPRINT",FACE,{"disambiguationData":[TD([[makeQuery(id+"F4.imprint","IMPRINT",EDGE,{"derivedFrom":sQuery(id+"F4.wireOp",EDGE,"E143.bottom")}),-1.0]])]});
            var Q3;
            Q3=makeQuery(id+"F4.imprint","IMPRINT",FACE,{"disambiguationData":[TD([[makeQuery(id+"F4.imprint","IMPRINT",EDGE,{"derivedFrom":sQuery(id+"F4.wireOp",EDGE,"E144.bottom")}),-1.0]])]});
            var Q4;
            Q4=makeQuery(id+"F4.imprint","IMPRINT",FACE,{"disambiguationData":[TD([[makeQuery(id+"F4.imprint","IMPRINT",EDGE,{"derivedFrom":sQuery(id+"F4.wireOp",EDGE,"E189.bottom")}),1.0]])]});
            var Q5;
            {var subQ3=sQuery(id+"F4.wireOp",EDGE,"MCrxn6Fo-NzhG-Mw8r-quQu-lXPODAZYxSbR");Q5=makeQuery(id+"F4.imprint","IMPRINT",FACE,{"disambiguationData":[TD([[makeQuery(id+"F4.imprint","IMPRINT",EDGE,{"derivedFrom":subQ3}),1.0]])]});}
            var Q6;
            Q6=makeQuery(id+"F4.imprint","IMPRINT",FACE,{"disambiguationData":[TD([[makeQuery(id+"F4.imprint","IMPRINT",EDGE,{"derivedFrom":sQuery(id+"F4.wireOp",EDGE,"kaJYNwhd-tLkA-7xD6-zw7H-YcnNiE7OrQMK.bottom")}),-1.0]])]});
            var Q7;
            Q7=makeQuery(id+"F4.imprint","IMPRINT",FACE,{"disambiguationData":[TD([[makeQuery(id+"F4.imprint","IMPRINT",EDGE,{"derivedFrom":sQuery(id+"F4.wireOp",EDGE,"E188.bottom")}),-1.0]])]});
            var Q8;
            Q8=makeQuery(id+"F4.imprint","IMPRINT",FACE,{"disambiguationData":[TD([[makeQuery(id+"F4.imprint","IMPRINT",EDGE,{"derivedFrom":sQuery(id+"F4.wireOp",EDGE,"E198.bottom")}),1.0]])]});
            var Q9;
            Q9=makeQuery(id+"F4.imprint","IMPRINT",FACE,{"disambiguationData":[TD([[makeQuery(id+"F4.imprint","IMPRINT",EDGE,{"derivedFrom":sQuery(id+"F4.wireOp",EDGE,"E197.bottom")}),1.0]])]});
            var Q10;
            Q10=makeQuery(id+"F4.imprint","IMPRINT",FACE,{"disambiguationData":[TD([[makeQuery(id+"F4.imprint","IMPRINT",EDGE,{"derivedFrom":sQuery(id+"F4.wireOp",EDGE,"E196.bottom")}),1.0]])]});
            var Q11;
            Q11=makeQuery(id+"F4.imprint","IMPRINT",FACE,{"disambiguationData":[TD([[makeQuery(id+"F4.imprint","IMPRINT",EDGE,{"derivedFrom":sQuery(id+"F4.wireOp",EDGE,"E191.bottom")}),-1.0]])]});
            var Q12;
            Q12=makeQuery(id+"F4.imprint","IMPRINT",FACE,{"disambiguationData":[TD([[makeQuery(id+"F4.imprint","IMPRINT",EDGE,{"derivedFrom":sQuery(id+"F4.wireOp",EDGE,"E192")}),1.0]])]});
            var Q13;
            Q13=makeQuery(id+"F4.imprint","IMPRINT",FACE,{"disambiguationData":[TD([[makeQuery(id+"F4.imprint","IMPRINT",EDGE,{"derivedFrom":sQuery(id+"F4.wireOp",EDGE,"E190.bottom")}),-1.0]])]});
            var Q14;
            Q14=makeQuery(id+"F4.imprint","IMPRINT",FACE,{"disambiguationData":[TD([[makeQuery(id+"F4.imprint","IMPRINT",EDGE,{"derivedFrom":sQuery(id+"F4.wireOp",EDGE,"E181.bottom")}),1.0]])]});
            var Q15;
            Q15=makeQuery(id+"F4.imprint","IMPRINT",FACE,{"disambiguationData":[TD([[makeQuery(id+"F4.imprint","IMPRINT",EDGE,{"derivedFrom":sQuery(id+"F4.wireOp",EDGE,"E174")}),1.0]])]});
            var Q16;
            Q16=makeQuery(id+"F4.imprint","IMPRINT",FACE,{"disambiguationData":[TD([[makeQuery(id+"F4.imprint","IMPRINT",EDGE,{"derivedFrom":sQuery(id+"F4.wireOp",EDGE,"E199")}),1.0]])]});
            var Q17;
            Q17=makeQuery(id+"F4.imprint","IMPRINT",FACE,{"disambiguationData":[TD([[makeQuery(id+"F4.imprint","IMPRINT",EDGE,{"derivedFrom":sQuery(id+"F4.wireOp",EDGE,"E200.bottom")}),1.0]])]});
            var Q18;
            Q18=makeQuery(id+"F4.imprint","IMPRINT",FACE,{"disambiguationData":[TD([[makeQuery(id+"F4.imprint","IMPRINT",EDGE,{"derivedFrom":sQuery(id+"F4.wireOp",EDGE,"E203.bottom")}),-1.0]])]});
            var Q19;
            {var subQ2=sQuery(id+"F4.wireOp",EDGE,"E240");Q19=makeQuery(id+"F4.imprint","IMPRINT",FACE,{"disambiguationData":[TD([[makeQuery(id+"F4.imprint","IMPRINT",EDGE,{"derivedFrom":subQ2}),-1.0]])]});}
            var Q20;
            Q20=makeQuery(id+"F4.imprint","IMPRINT",FACE,{"disambiguationData":[TD([[makeQuery(id+"F4.imprint","IMPRINT",EDGE,{"derivedFrom":sQuery(id+"F4.wireOp",EDGE,"scah6wH5-Tskl-Ngyk-Nis7-oLGqzMOM8Rne")}),-1.0]])]});
            var Q21;
            {var subQ5=sQuery(id+"F4.wireOp",EDGE,"E262");Q21=makeQuery(id+"F4.imprint","IMPRINT",FACE,{"disambiguationData":[TD([[makeQuery(id+"F4.imprint","IMPRINT",EDGE,{"derivedFrom":subQ5}),-1.0]])]});}
            var Q22;
            {var subQ0=sQuery(id+"F4.wireOp",EDGE,"E269");Q22=makeQuery(id+"F4.imprint","IMPRINT",FACE,{"disambiguationData":[TD([[makeQuery(id+"F4.imprint","IMPRINT",EDGE,{"derivedFrom":subQ0}),1.0]])]});}
            extrude(context, id + "F6", {"entities" : qUnion([Q0, Q1, Q2, Q3, Q4, Q5, Q6, Q7, Q8, Q9, Q10, Q11, Q12, Q13, Q14, Q15, Q16, Q17, Q18, Q19, Q20, Q21, Q22]), "depth" : 1219.2 * mm, "offsetDistance" : 25.4 * mm});
        }
        {
            var Q0;
            Q0=makeQuery(id+"F4.imprint","IMPRINT",FACE,{"disambiguationData":[TD([[makeQuery(id+"F4.imprint","IMPRINT",EDGE,{"derivedFrom":sQuery(id+"F4.wireOp",EDGE,"OWgZVGeK-I4Oq-mPDz-53rv-7XKkJ5bVqfe1")}),-1.0]])]});
            var Q1;
            {var subQ3=sQuery(id+"F4.wireOp",EDGE,"E151");Q1=makeQuery(id+"F4.imprint","IMPRINT",FACE,{"disambiguationData":[TD([[makeQuery(id+"F4.imprint","IMPRINT",EDGE,{"derivedFrom":subQ3}),1.0]])]});}
            var Q2;
            Q2=makeQuery(id+"F4.imprint","IMPRINT",FACE,{"disambiguationData":[TD([[makeQuery(id+"F4.imprint","IMPRINT",EDGE,{"derivedFrom":sQuery(id+"F4.wireOp",EDGE,"OHAR3kxy-Vky0-QxAG-91pp-j2nMnPBeihf4")}),-1.0]])]});
            var Q3;
            {var subQ0=sQuery(id+"F4.wireOp",EDGE,"RL9BpvKr-ViOR-KplK-dQ8D-cPNKQByL2L34");Q3=makeQuery(id+"F4.imprint","IMPRINT",FACE,{"disambiguationData":[TD([[makeQuery(id+"F4.imprint","IMPRINT",EDGE,{"derivedFrom":subQ0}),-1.0]])]});}
            var Q4;
            {var subQ0=sQuery(id+"F4.wireOp",EDGE,"E243");Q4=makeQuery(id+"F4.imprint","IMPRINT",FACE,{"disambiguationData":[TD([[makeQuery(id+"F4.imprint","IMPRINT",EDGE,{"derivedFrom":subQ0}),1.0]])]});}
            var Q5;
            {var subQ2=sQuery(id+"F4.wireOp",EDGE,"E239");Q5=makeQuery(id+"F4.imprint","IMPRINT",FACE,{"disambiguationData":[TD([[makeQuery(id+"F4.imprint","IMPRINT",EDGE,{"derivedFrom":subQ2}),1.0]])]});}
            var Q6;
            {var subQ1=sQuery(id+"F4.wireOp",EDGE,"E251");Q6=makeQuery(id+"F4.imprint","IMPRINT",FACE,{"disambiguationData":[TD([[makeQuery(id+"F4.imprint","IMPRINT",EDGE,{"derivedFrom":subQ1}),-1.0]])]});}
            var Q7;
            {var subQ0=sQuery(id+"F4.wireOp",EDGE,"E262");Q7=makeQuery(id+"F4.imprint","IMPRINT",FACE,{"disambiguationData":[TD([[makeQuery(id+"F4.imprint","IMPRINT",EDGE,{"derivedFrom":subQ0}),1.0]])]});}
            var Q8;
            {var subQ0=sQuery(id+"F4.wireOp",EDGE,"E269");Q8=makeQuery(id+"F4.imprint","IMPRINT",FACE,{"disambiguationData":[TD([[makeQuery(id+"F4.imprint","IMPRINT",EDGE,{"derivedFrom":subQ0}),-1.0]])]});}
            extrude(context, id + "F7", {"entities" : qUnion([Q0, Q1, Q2, Q3, Q4, Q5, Q6, Q7, Q8]), "depth" : 914.4 * mm, "offsetDistance" : 25.4 * mm});
        }
        {
            var Q0;
            Q0=qCreatedBy(makeId("Top.planeOp"),FACE);
            var sketch = newSketch(context, id + "F8", { "sketchPlane" : qUnion([Q0])});
            skLineSegment(sketch, "E280", {"start": v(1230.3, -3796.55) * mm, "end": v(1916.1, -3796.55) * mm});
            skLineSegment(sketch, "E281", {"start": v(1230.3, -3796.55) * mm, "end": v(1230.3, -3707.65) * mm});
            skLineSegment(sketch, "E282", {"start": v(1230.3, -3707.65) * mm, "end": v(1916.1, -3707.65) * mm});
            skLineSegment(sketch, "E283", {"start": v(1916.1, -3707.65) * mm, "end": v(1916.1, -3796.55) * mm});
            skLineSegment(sketch, "E284.bottom", {"start": v(318.25, -5828.55) * mm, "end": v(1385.05, -5828.55) * mm});
            skLineSegment(sketch, "E284.top", {"start": v(318.25, -7657.35) * mm, "end": v(1385.05, -7657.35) * mm});
            skLineSegment(sketch, "E284.left", {"start": v(318.25, -5828.55) * mm, "end": v(318.25, -7657.35) * mm});
            skLineSegment(sketch, "E284.right", {"start": v(1385.05, -5828.55) * mm, "end": v(1385.05, -7657.35) * mm});
            skLineSegment(sketch, "E285.top", {"start": v(-1370.85, -7504.95) * mm, "end": v(-1205.75, -7504.95) * mm});
            skLineSegment(sketch, "E285.left", {"start": v(-1294.65, -5165.84) * mm, "end": v(-1294.65, -7416.05) * mm});
            skLineSegment(sketch, "E285.right", {"start": v(-1205.75, -5202.66) * mm, "end": v(-1205.75, -7504.95) * mm});
            skArc(sketch, "E286", {"start": v(-2296.14, -4622.73) * mm, "mid": v(-1121.06, -4829.91) * mm, "end": v(-524.5, -3796.55) * mm, "construction": true});
            skLineSegment(sketch, "E287", {"start": v(-1294.65, -5165.84) * mm, "end": v(-520.54, -4391.73) * mm});
            skLineSegment(sketch, "E288", {"start": v(-1205.75, -5202.66) * mm, "end": v(-431.64, -4428.56) * mm});
            skLineSegment(sketch, "E289.bottom", {"start": v(-520.54, -3796.55) * mm, "end": v(-431.64, -3796.55) * mm});
            skLineSegment(sketch, "E289.left", {"start": v(-520.54, -3796.55) * mm, "end": v(-520.54, -4391.73) * mm});
            skLineSegment(sketch, "E289.right", {"start": v(-431.64, -3796.55) * mm, "end": v(-431.64, -4428.56) * mm});
            skLineSegment(sketch, "E290", {"start": v(-1294.65, -7416.05) * mm, "end": v(-1370.85, -7416.05) * mm});
            skLineSegment(sketch, "E291", {"start": v(-1370.85, -7416.05) * mm, "end": v(-1370.85, -7504.95) * mm});
            skLineSegment(sketch, "E292.bottom", {"start": v(-2386.85, -7504.95) * mm, "end": v(-2310.65, -7504.95) * mm});
            skLineSegment(sketch, "E292.top", {"start": v(-2386.85, -7416.05) * mm, "end": v(-2310.65, -7416.05) * mm});
            skLineSegment(sketch, "E292.left", {"start": v(-2386.85, -7504.95) * mm, "end": v(-2386.85, -7416.05) * mm});
            skLineSegment(sketch, "E292.right", {"start": v(-2310.65, -7504.95) * mm, "end": v(-2310.65, -7416.05) * mm});
            skLineSegment(sketch, "E293.bottom", {"start": v(2942.55, -1569.88) * mm, "end": v(3856.95, -1569.88) * mm});
            skLineSegment(sketch, "E293.top", {"start": v(3018.75, -2027.08) * mm, "end": v(3780.75, -2027.08) * mm});
            skLineSegment(sketch, "E293.left", {"start": v(2942.55, -1569.88) * mm, "end": v(2942.55, -1874.68) * mm});
            skLineSegment(sketch, "E293.right", {"start": v(3856.95, -1569.88) * mm, "end": v(3856.95, -1874.68) * mm});
            skLineSegment(sketch, "E294", {"start": v(2942.55, -1874.68) * mm, "end": v(3018.75, -1874.68) * mm});
            skLineSegment(sketch, "E295", {"start": v(3018.75, -1874.68) * mm, "end": v(3018.75, -2027.08) * mm});
            skLineSegment(sketch, "E296", {"start": v(3780.75, -2027.08) * mm, "end": v(3780.75, -1874.68) * mm});
            skLineSegment(sketch, "E297", {"start": v(3780.75, -1874.68) * mm, "end": v(3856.95, -1874.68) * mm});
            skLineSegment(sketch, "E298.bottom", {"start": v(-1180.35, -7156.2) * mm, "end": v(-570.75, -7156.2) * mm});
            skLineSegment(sketch, "E298.top", {"start": v(-1180.35, -5632.2) * mm, "end": v(-570.75, -5632.2) * mm});
            skLineSegment(sketch, "E298.left", {"start": v(-1180.35, -7156.2) * mm, "end": v(-1180.35, -5632.2) * mm});
            skLineSegment(sketch, "E298.right", {"start": v(-570.75, -7156.2) * mm, "end": v(-570.75, -5632.2) * mm});
            skLineSegment(sketch, "E299.bottom", {"start": v(-338.96, -3821.95) * mm, "end": v(1667.64, -3821.95) * mm});
            skLineSegment(sketch, "E299.top", {"start": v(-338.96, -4533.15) * mm, "end": v(1667.64, -4533.15) * mm});
            skLineSegment(sketch, "E299.left", {"start": v(-338.96, -3821.95) * mm, "end": v(-338.96, -4533.15) * mm});
            skLineSegment(sketch, "E299.right", {"start": v(1667.64, -3821.95) * mm, "end": v(1667.64, -4533.15) * mm});
            skLineSegment(sketch, "E300", {"start": v(3338.5, -4013.5) * mm, "end": v(4199.54, -4874.55) * mm, "construction": true});
            skLineSegment(sketch, "E301", {"start": v(3338.5, -4013.5) * mm, "end": v(3338.5, -3150.34) * mm, "construction": true});
            skLineSegment(sketch, "E302", {"start": v(3338.5, -3150.34) * mm, "end": v(3984.02, -3150.34) * mm});
            skLineSegment(sketch, "E303", {"start": v(3984.02, -3150.34) * mm, "end": v(5062.7, -4229.03) * mm});
            skLineSegment(sketch, "E304", {"start": v(5062.7, -4229.03) * mm, "end": v(5062.7, -4874.55) * mm});
            skLineSegment(sketch, "E305", {"start": v(5062.7, -4874.55) * mm, "end": v(4199.54, -4874.55) * mm, "construction": true});
            skLineSegment(sketch, "E306.bottom", {"start": v(1243, -3694.95) * mm, "end": v(1852.6, -3694.95) * mm});
            skLineSegment(sketch, "E306.top", {"start": v(1243, -1473.94) * mm, "end": v(1852.6, -1473.94) * mm});
            skLineSegment(sketch, "E306.left", {"start": v(1243, -3694.95) * mm, "end": v(1243, -1473.94) * mm});
            skLineSegment(sketch, "E306.right", {"start": v(1852.6, -3694.95) * mm, "end": v(1852.6, -1473.94) * mm});
            skLineSegment(sketch, "E307.bottom", {"start": v(1230.3, -1321.54) * mm, "end": v(2005, -1321.54) * mm});
            skLineSegment(sketch, "E307.top", {"start": v(1230.3, -1461.24) * mm, "end": v(2005, -1461.24) * mm});
            skLineSegment(sketch, "E307.left", {"start": v(1230.3, -1321.54) * mm, "end": v(1230.3, -1461.24) * mm});
            skLineSegment(sketch, "E307.right", {"start": v(2005, -1321.54) * mm, "end": v(2005, -1461.24) * mm});
            skLineSegment(sketch, "E308", {"start": v(4741.53, -1321.54) * mm, "end": v(2970.2, -1321.54) * mm});
            skLineSegment(sketch, "E309", {"start": v(2970.2, -1321.54) * mm, "end": v(2970.2, -1461.24) * mm});
            skLineSegment(sketch, "E310", {"start": v(2970.2, -1461.24) * mm, "end": v(4683.66, -1461.24) * mm});
            skLineSegment(sketch, "E311.bottom", {"start": v(4044.9, -1473.94) * mm, "end": v(4678.4, -1473.94) * mm});
            skLineSegment(sketch, "E311.top", {"start": v(4044.9, -2083.54) * mm, "end": v(4425.9, -2083.54) * mm});
            skLineSegment(sketch, "E311.left", {"start": v(4044.9, -1473.94) * mm, "end": v(4044.9, -2083.54) * mm});
            skLineSegment(sketch, "E312.0", {"start": v(3135.3, -4097.67) * mm, "end": v(3135.3, -3353.54) * mm});
            skLineSegment(sketch, "E312.1", {"start": v(3135.3, -4097.67) * mm, "end": v(4115.37, -5077.75) * mm});
            skLineSegment(sketch, "E312.2", {"start": v(4859.5, -5077.75) * mm, "end": v(4115.37, -5077.75) * mm});
            skLineSegment(sketch, "E313.0", {"start": v(3541.7, -3929.34) * mm, "end": v(3541.7, -3150.34) * mm});
            skLineSegment(sketch, "E313.1", {"start": v(3541.7, -3929.34) * mm, "end": v(4283.71, -4671.35) * mm});
            skLineSegment(sketch, "E313.2", {"start": v(5062.7, -4671.35) * mm, "end": v(4283.71, -4671.35) * mm});
            skLineSegment(sketch, "E314", {"start": v(3338.5, -3150.34) * mm, "end": v(3135.3, -3353.54) * mm});
            skLineSegment(sketch, "E315", {"start": v(5062.7, -4874.55) * mm, "end": v(4859.5, -5077.75) * mm});
            skLineSegment(sketch, "E316.bottom", {"start": v(5638.83, -7136.19) * mm, "end": v(6975.23, -5799.78) * mm});
            skLineSegment(sketch, "E316.top", {"start": v(5207.77, -6705.14) * mm, "end": v(5341.89, -6571.03) * mm});
            skLineSegment(sketch, "E316.left", {"start": v(5638.83, -7136.19) * mm, "end": v(5207.77, -6705.14) * mm});
            skLineSegment(sketch, "E317", {"start": v(5341.89, -6571.03) * mm, "end": v(5108.4, -6337.54) * mm});
            skLineSegment(sketch, "E318", {"start": v(5108.4, -6337.54) * mm, "end": v(5754.98, -5690.96) * mm});
            skLineSegment(sketch, "E319", {"start": v(5754.98, -5690.96) * mm, "end": v(5988.46, -5924.45) * mm});
            skLineSegment(sketch, "E320.trimOffspring", {"start": v(5988.46, -5924.45) * mm, "end": v(6365.63, -5547.28) * mm});
            skLineSegment(sketch, "E321.bottom", {"start": v(4678.4, -1473.94) * mm, "end": v(6975.23, -3770.77) * mm});
            skLineSegment(sketch, "E321.top", {"start": v(4425.9, -2083.54) * mm, "end": v(6365.63, -4023.28) * mm});
            skLineSegment(sketch, "E322", {"start": v(6365.63, -4023.28) * mm, "end": v(6365.63, -5547.28) * mm});
            skLineSegment(sketch, "E323", {"start": v(6975.23, -3770.77) * mm, "end": v(6975.23, -5799.78) * mm});
            skLineSegment(sketch, "E324.bottom", {"start": v(6391.03, -4328.08) * mm, "end": v(6899.03, -4328.08) * mm, "construction": true});
            skLineSegment(sketch, "E324.top", {"start": v(6391.03, -5242.48) * mm, "end": v(6899.03, -5242.48) * mm, "construction": true});
            skLineSegment(sketch, "E324.left", {"start": v(6391.03, -4328.08) * mm, "end": v(6391.03, -5242.48) * mm, "construction": true});
            skLineSegment(sketch, "E324.right", {"start": v(6899.03, -4328.08) * mm, "end": v(6899.03, -5242.48) * mm, "construction": true});
            skLineSegment(sketch, "E325", {"start": v(6899.03, -4785.28) * mm, "end": v(6975.23, -4785.28) * mm, "construction": true});
            skLineSegment(sketch, "E326", {"start": v(4683.66, -1461.24) * mm, "end": v(6987.93, -3765.51) * mm});
            skLineSegment(sketch, "E327", {"start": v(6987.93, -3765.51) * mm, "end": v(6987.93, -5805.04) * mm});
            skLineSegment(sketch, "E328", {"start": v(6987.93, -5805.04) * mm, "end": v(5647.8, -7145.17) * mm});
            skLineSegment(sketch, "E329", {"start": v(5647.8, -7145.17) * mm, "end": v(5710.67, -7208.03) * mm});
            skLineSegment(sketch, "E330", {"start": v(5710.67, -7208.03) * mm, "end": v(7127.63, -5791.07) * mm});
            skLineSegment(sketch, "E331", {"start": v(7127.63, -5791.07) * mm, "end": v(7127.63, -3707.65) * mm});
            skLineSegment(sketch, "E332", {"start": v(7127.63, -3707.65) * mm, "end": v(4741.53, -1321.54) * mm});
            skLineSegment(sketch, "E333.bottom", {"start": v(5305.96, -2173.34) * mm, "end": v(5844.78, -2712.16) * mm});
            skLineSegment(sketch, "E333.top", {"start": v(4946.75, -2532.55) * mm, "end": v(5485.57, -3071.37) * mm});
            skLineSegment(sketch, "E333.left", {"start": v(5198.2, -2173.34) * mm, "end": v(4946.75, -2424.8) * mm});
            skLineSegment(sketch, "E333.right", {"start": v(5844.78, -2819.92) * mm, "end": v(5593.33, -3071.37) * mm});
            skPoint(sketch, "E334.visualSharp", {"position": v(5252.08, -2119.46) * mm});
            skArc(sketch, "E334.filletArc", {"start": v(5305.96, -2173.34) * mm, "mid": v(5252.08, -2151.03) * mm, "end": v(5198.2, -2173.34) * mm});
            skPoint(sketch, "E335.visualSharp", {"position": v(4892.87, -2478.67) * mm});
            skArc(sketch, "E335.filletArc", {"start": v(4946.75, -2424.8) * mm, "mid": v(4924.44, -2478.67) * mm, "end": v(4946.75, -2532.55) * mm});
            skPoint(sketch, "E336.visualSharp", {"position": v(5539.45, -3125.25) * mm});
            skArc(sketch, "E336.filletArc", {"start": v(5485.57, -3071.37) * mm, "mid": v(5539.45, -3093.69) * mm, "end": v(5593.33, -3071.37) * mm});
            skPoint(sketch, "E337.visualSharp", {"position": v(5898.66, -2766.04) * mm});
            skArc(sketch, "E337.filletArc", {"start": v(5844.78, -2819.92) * mm, "mid": v(5867.1, -2766.04) * mm, "end": v(5844.78, -2712.16) * mm});
            skCircle(sketch, "E338", {"center": v(6505.33, -4442.38) * mm, "radius": 114.3 * mm});
            skCircle(sketch, "E339", {"center": v(6784.73, -4442.38) * mm, "radius": 114.3 * mm});
            skCircle(sketch, "E340", {"center": v(6505.33, -4785.28) * mm, "radius": 114.3 * mm});
            skCircle(sketch, "E341", {"center": v(6784.73, -4785.28) * mm, "radius": 114.3 * mm});
            skCircle(sketch, "E342", {"center": v(6505.33, -5128.18) * mm, "radius": 114.3 * mm});
            skCircle(sketch, "E343", {"center": v(6784.73, -5128.18) * mm, "radius": 114.3 * mm});
            skLineSegment(sketch, "E344", {"start": v(6505.33, -4442.38) * mm, "end": v(6505.33, -4785.28) * mm, "construction": true});
            skLineSegment(sketch, "E345", {"start": v(6505.33, -4785.28) * mm, "end": v(6505.33, -5128.18) * mm, "construction": true});
            skLineSegment(sketch, "E346", {"start": v(6784.73, -4442.38) * mm, "end": v(6784.73, -4785.28) * mm, "construction": true});
            skLineSegment(sketch, "E347", {"start": v(6784.73, -4785.28) * mm, "end": v(6784.73, -5128.18) * mm, "construction": true});
            skLineSegment(sketch, "E348", {"start": v(1852.6, -3694.95) * mm, "end": v(1852.6, -3694.95) * mm});
            skLineSegment(sketch, "E349", {"start": v(1852.6, -3694.95) * mm, "end": v(1852.6, -2780.55) * mm});
            skLineSegment(sketch, "E350", {"start": v(1852.6, -2780.55) * mm, "end": v(1852.6, -2780.55) * mm});
            skLineSegment(sketch, "E351", {"start": v(2005, -1461.24) * mm, "end": v(2970.2, -1461.24) * mm});
            skLineSegment(sketch, "E352", {"start": v(2005, -1454.9) * mm, "end": v(2970.2, -1454.9) * mm});
            skSolve(sketch);
        }
        {
            var Q0;
            Q0=makeQuery(id+"F8.imprint","IMPRINT",FACE,{"disambiguationData":[TD([[makeQuery(id+"F8.imprint","IMPRINT",EDGE,{"derivedFrom":sQuery(id+"F8.wireOp",EDGE,"E280")}),1.0]])]});
            var Q1;
            Q1=makeQuery(id+"F8.imprint","IMPRINT",FACE,{"disambiguationData":[TD([[makeQuery(id+"F8.imprint","IMPRINT",EDGE,{"derivedFrom":sQuery(id+"F8.wireOp",EDGE,"E307.bottom")}),-1.0]])]});
            var Q2;
            Q2=makeQuery(id+"F8.imprint","IMPRINT",FACE,{"disambiguationData":[TD([[makeQuery(id+"F8.imprint","IMPRINT",EDGE,{"derivedFrom":sQuery(id+"F8.wireOp",EDGE,"E308")}),1.0]])]});
            var Q3;
            Q3=makeQuery(id+"F8.imprint","IMPRINT",FACE,{"disambiguationData":[TD([[makeQuery(id+"F8.imprint","IMPRINT",EDGE,{"derivedFrom":sQuery(id+"F8.wireOp",EDGE,"E285.top")}),1.0]])]});
            var Q4;
            Q4=makeQuery(id+"F8.imprint","IMPRINT",FACE,{"disambiguationData":[TD([[makeQuery(id+"F8.imprint","IMPRINT",EDGE,{"derivedFrom":sQuery(id+"F8.wireOp",EDGE,"E292.bottom")}),1.0]])]});
            var Q5;
            {var subQ0=sQuery(id+"F8.wireOp",EDGE,"E351");Q5=makeQuery(id+"F8.imprint","IMPRINT",FACE,{"disambiguationData":[TD([[makeQuery(id+"F8.imprint","IMPRINT",EDGE,{"derivedFrom":subQ0}),1.0]])]});}
            extrude(context, id + "F9", {"entities" : qUnion([Q0, Q1, Q2, Q3, Q4, Q5]), "operationType" : NewBodyOperationType.ADD, "depth" : 2466.97 * mm, "offsetDistance" : 25.4 * mm});
        }
        {
            var Q0;
            Q0=makeQuery(id+"F8.imprint","IMPRINT",FACE,{"disambiguationData":[TD([[makeQuery(id+"F8.imprint","IMPRINT",EDGE,{"derivedFrom":sQuery(id+"F8.wireOp",EDGE,"E298.bottom")}),1.0]])]});
            var Q1;
            Q1=makeQuery(id+"F8.imprint","IMPRINT",FACE,{"disambiguationData":[TD([[makeQuery(id+"F8.imprint","IMPRINT",EDGE,{"derivedFrom":sQuery(id+"F8.wireOp",EDGE,"E284.bottom")}),-1.0]])]});
            var Q2;
            Q2=makeQuery(id+"F8.imprint","IMPRINT",FACE,{"disambiguationData":[TD([[makeQuery(id+"F8.imprint","IMPRINT",EDGE,{"derivedFrom":sQuery(id+"F8.wireOp",EDGE,"E299.bottom")}),-1.0]])]});
            var Q3;
            Q3=makeQuery(id+"F8.imprint","IMPRINT",FACE,{"disambiguationData":[TD([[makeQuery(id+"F8.imprint","IMPRINT",EDGE,{"derivedFrom":sQuery(id+"F8.wireOp",EDGE,"E306.bottom")}),1.0]])]});
            var Q4;
            Q4=makeQuery(id+"F8.imprint","IMPRINT",FACE,{"disambiguationData":[TD([[makeQuery(id+"F8.imprint","IMPRINT",EDGE,{"derivedFrom":sQuery(id+"F8.wireOp",EDGE,"E311.bottom")}),-1.0]])]});
            var Q5;
            Q5=makeQuery(id+"F8.imprint","IMPRINT",FACE,{"disambiguationData":[TD([[makeQuery(id+"F8.imprint","IMPRINT",EDGE,{"derivedFrom":sQuery(id+"F8.wireOp",EDGE,"E312.0")}),-1.0]])]});
            var Q6;
            {var subQ0=sQuery(id+"F8.wireOp",EDGE,"E348");Q6=makeQuery(id+"F8.imprint","IMPRINT",FACE,{"disambiguationData":[TD([[makeQuery(id+"F8.imprint","IMPRINT",EDGE,{"derivedFrom":subQ0}),1.0]])]});}
            var Q7;
            {var subQ6=sQuery(id+"F8.wireOp",EDGE,"E299.top");Q7=makeQuery(id+"F8.imprint","IMPRINT",FACE,{"disambiguationData":[TD([[makeQuery(id+"F8.imprint","IMPRINT",EDGE,{"derivedFrom":subQ6}),1.0]])]});}
            extrude(context, id + "F10", {"entities" : qUnion([Q0, Q1, Q2, Q3, Q4, Q5, Q6, Q7]), "depth" : 914.4 * mm, "offsetDistance" : 25.4 * mm});
        }
        {
            var Q0;
            {var subQ1=sQuery(id+"F8.wireOp",EDGE,"E303");Q0=makeQuery(id+"F8.imprint","IMPRINT",FACE,{"disambiguationData":[TD([[makeQuery(id+"F8.imprint","IMPRINT",EDGE,{"derivedFrom":subQ1}),-1.0]])]});}
            var Q1;
            Q1=makeQuery(id+"F8.imprint","IMPRINT",FACE,{"disambiguationData":[TD([[makeQuery(id+"F8.imprint","IMPRINT",EDGE,{"derivedFrom":sQuery(id+"F8.wireOp",EDGE,"E293.bottom")}),-1.0]])]});
            extrude(context, id + "F11", {"entities" : qUnion([Q0, Q1]), "depth" : 609.6 * mm, "offsetDistance" : 25.4 * mm});
        }
        {
            var Q0;
            Q0=qCreatedBy(makeId("Top.planeOp"),FACE);
            var sketch = newSketch(context, id + "F12", { "sketchPlane" : qUnion([Q0])});
            skLineSegment(sketch, "E353", {"start": v(8396.77, -7257.77) * mm, "end": v(7028.85, -5889.85) * mm});
            skLineSegment(sketch, "E354", {"start": v(7028.85, -5889.85) * mm, "end": v(7127.63, -5791.07) * mm});
            skLineSegment(sketch, "E355", {"start": v(7127.63, -5791.07) * mm, "end": v(10614.9, -9278.32) * mm});
            skLineSegment(sketch, "E356", {"start": v(5710.67, -7208.03) * mm, "end": v(6107.26, -7604.62) * mm});
            skLineSegment(sketch, "E357", {"start": v(6107.26, -7604.62) * mm, "end": v(6170.12, -7541.76) * mm});
            skLineSegment(sketch, "E358", {"start": v(6170.12, -7541.76) * mm, "end": v(5773.53, -7145.17) * mm});
            skLineSegment(sketch, "E359", {"start": v(5773.53, -7145.17) * mm, "end": v(5710.67, -7208.03) * mm});
            skLineSegment(sketch, "E360", {"start": v(7527.6, -10695.29) * mm, "end": v(7042.67, -10210.36) * mm});
            skLineSegment(sketch, "E361", {"start": v(5229.1, -8396.79) * mm, "end": v(5229.1, -8271.06) * mm});
            skLineSegment(sketch, "E362", {"start": v(5229.1, -8271.06) * mm, "end": v(6566.71, -9608.68) * mm});
            skLineSegment(sketch, "E363.bottom", {"start": v(5254.5, -10670.15) * mm, "end": v(5940.3, -10670.15) * mm});
            skLineSegment(sketch, "E363.top", {"start": v(5254.5, -10314.55) * mm, "end": v(5940.3, -10314.55) * mm});
            skLineSegment(sketch, "E363.left", {"start": v(5254.5, -10670.15) * mm, "end": v(5254.5, -10314.55) * mm});
            skLineSegment(sketch, "E363.right", {"start": v(5940.3, -10670.15) * mm, "end": v(5940.3, -10314.55) * mm});
            skLineSegment(sketch, "E364", {"start": v(5940.3, -9107.99) * mm, "end": v(5229.1, -9107.99) * mm});
            skLineSegment(sketch, "E365.bottom", {"start": v(5356.1, -9133.39) * mm, "end": v(5864.1, -9133.39) * mm});
            skLineSegment(sketch, "E365.top", {"start": v(5356.1, -9361.99) * mm, "end": v(5864.1, -9361.99) * mm});
            skLineSegment(sketch, "E365.left", {"start": v(5356.1, -9133.39) * mm, "end": v(5356.1, -9361.99) * mm});
            skLineSegment(sketch, "E365.right", {"start": v(5864.1, -9133.39) * mm, "end": v(5864.1, -9361.99) * mm});
            skEllipse(sketch, "E366", {"center": v(5610.1, -9628.69) * mm, "majorRadius": 266.7 * mm, "minorRadius": 203.2 * mm, "majorAxis": v(0, 1)});
            skLineSegment(sketch, "E367", {"start": v(5610.1, -9628.69) * mm, "end": v(5610.1, -9361.99) * mm, "construction": true});
            skLineSegment(sketch, "E368", {"start": v(5610.1, -9628.69) * mm, "end": v(5610.1, -9895.39) * mm, "construction": true});
            skLineSegment(sketch, "E369", {"start": v(6503.85, -9671.54) * mm, "end": v(6566.71, -9608.68) * mm});
            skLineSegment(sketch, "E370", {"start": v(7042.67, -10210.36) * mm, "end": v(7105.53, -10147.5) * mm});
            skLineSegment(sketch, "E371.trimOffspring", {"start": v(7105.53, -10147.5) * mm, "end": v(7590.46, -10632.43) * mm});
            skLineSegment(sketch, "E372.trimOffspring", {"start": v(6503.85, -9671.54) * mm, "end": v(5940.3, -9107.99) * mm});
            skArc(sketch, "E373", {"start": v(7042.67, -10210.36) * mm, "mid": v(6280.13, -10399.96) * mm, "end": v(5755.48, -9815.01) * mm, "construction": true});
            skLineSegment(sketch, "E374", {"start": v(7527.6, -10695.29) * mm, "end": v(6759.22, -11463.67) * mm});
            skLineSegment(sketch, "E375", {"start": v(7689.24, -10731.21) * mm, "end": v(6858, -11562.45) * mm});
            skLineSegment(sketch, "E376", {"start": v(6759.22, -11463.67) * mm, "end": v(6858, -11562.45) * mm});
            skLineSegment(sketch, "E377", {"start": v(6460.9, -10935.8) * mm, "end": v(6856.04, -11330.93) * mm});
            skLineSegment(sketch, "E378", {"start": v(6856.04, -11330.93) * mm, "end": v(7394.86, -10792.11) * mm});
            skLineSegment(sketch, "E379", {"start": v(7394.86, -10792.11) * mm, "end": v(6999.73, -10396.98) * mm});
            skLineSegment(sketch, "E380", {"start": v(6999.73, -10396.98) * mm, "end": v(6460.9, -10935.8) * mm});
            skLineSegment(sketch, "E381", {"start": v(7394.86, -10792.11) * mm, "end": v(7527.6, -10695.29) * mm, "construction": true});
            skLineSegment(sketch, "E382", {"start": v(6856.04, -11330.93) * mm, "end": v(6759.22, -11463.67) * mm, "construction": true});
            skLineSegment(sketch, "E383", {"start": v(6856.04, -11330.93) * mm, "end": v(6999.73, -10396.98) * mm, "construction": true});
            skEllipse(sketch, "E384", {"center": v(6927.88, -10863.95) * mm, "majorRadius": 304.8 * mm, "minorRadius": 203.2 * mm, "majorAxis": v(0.7, 0.7)});
            skLineSegment(sketch, "E385", {"start": v(6927.88, -10863.95) * mm, "end": v(7143.4, -10648.43) * mm, "construction": true});
            skLineSegment(sketch, "E386", {"start": v(8396.77, -7257.77) * mm, "end": v(7141.45, -8513.09) * mm});
            skLineSegment(sketch, "E387", {"start": v(6744.86, -8116.5) * mm, "end": v(6682, -8179.36) * mm});
            skLineSegment(sketch, "E388", {"start": v(6682, -8179.36) * mm, "end": v(7626.38, -9123.74) * mm});
            skLineSegment(sketch, "E389", {"start": v(7204.31, -8575.95) * mm, "end": v(8459.63, -7320.63) * mm});
            skLineSegment(sketch, "E390", {"start": v(8459.63, -7320.63) * mm, "end": v(10417.33, -9278.32) * mm});
            skLineSegment(sketch, "E391", {"start": v(9162, -10533.65) * mm, "end": v(10417.33, -9278.32) * mm});
            skLineSegment(sketch, "E392", {"start": v(9162, -10731.21) * mm, "end": v(8371.74, -11521.47) * mm});
            skLineSegment(sketch, "E393", {"start": v(7590.46, -10632.43) * mm, "end": v(7644.34, -10578.55) * mm});
            skLineSegment(sketch, "E394", {"start": v(7644.34, -10578.55) * mm, "end": v(7738.64, -10672.84) * mm});
            skLineSegment(sketch, "E395", {"start": v(7738.64, -10672.84) * mm, "end": v(8349.3, -10062.18) * mm});
            skLineSegment(sketch, "E396", {"start": v(8371.74, -11521.47) * mm, "end": v(7635.36, -10785.1) * mm});
            skLineSegment(sketch, "E397", {"start": v(9162, -10731.21) * mm, "end": v(10614.9, -9278.32) * mm});
            skLineSegment(sketch, "E398", {"start": v(5229.1, -9107.99) * mm, "end": v(5229.1, -9019.09) * mm});
            skLineSegment(sketch, "E399", {"start": v(5229.1, -9019.09) * mm, "end": v(5851.4, -9019.09) * mm});
            skLineSegment(sketch, "E400.trimOffspring", {"start": v(5851.4, -9019.09) * mm, "end": v(5229.1, -8396.79) * mm});
            skLineSegment(sketch, "E401", {"start": v(7626.38, -9123.74) * mm, "end": v(7689.24, -9060.88) * mm});
            skLineSegment(sketch, "E402", {"start": v(7204.31, -8575.95) * mm, "end": v(7635.36, -9007) * mm});
            skLineSegment(sketch, "E403", {"start": v(7635.36, -9007) * mm, "end": v(8890.68, -7751.68) * mm});
            skLineSegment(sketch, "E404.bottom", {"start": v(8614.21, -9931.97) * mm, "end": v(9153.03, -10470.78) * mm});
            skLineSegment(sketch, "E404.top", {"start": v(9153.03, -9393.15) * mm, "end": v(9691.84, -9931.97) * mm});
            skLineSegment(sketch, "E404.left", {"start": v(8614.21, -9931.97) * mm, "end": v(9153.03, -9393.15) * mm});
            skLineSegment(sketch, "E404.right", {"start": v(9153.03, -10470.78) * mm, "end": v(9691.84, -9931.97) * mm});
            skLineSegment(sketch, "E405.bottom", {"start": v(9276.84, -9269.34) * mm, "end": v(9815.65, -9808.16) * mm});
            skLineSegment(sketch, "E405.top", {"start": v(9815.65, -8730.53) * mm, "end": v(10354.47, -9269.34) * mm});
            skLineSegment(sketch, "E405.left", {"start": v(9276.84, -9269.34) * mm, "end": v(9815.65, -8730.53) * mm});
            skLineSegment(sketch, "E405.right", {"start": v(9815.65, -9808.16) * mm, "end": v(10354.47, -9269.34) * mm});
            skLineSegment(sketch, "E406", {"start": v(7028.85, -6464.58) * mm, "end": v(7822.03, -7257.77) * mm});
            skLineSegment(sketch, "E407", {"start": v(7822.03, -7257.77) * mm, "end": v(7141.45, -7938.35) * mm});
            skLineSegment(sketch, "E408", {"start": v(5773.53, -7145.17) * mm, "end": v(7028.85, -5889.85) * mm});
            skLineSegment(sketch, "E409", {"start": v(7689.24, -9060.88) * mm, "end": v(7204.31, -8575.95) * mm});
            skLineSegment(sketch, "E410", {"start": v(8169.69, -11319.42) * mm, "end": v(8959.95, -10529.16) * mm});
            skLineSegment(sketch, "E411", {"start": v(8757.9, -10327.1) * mm, "end": v(7967.63, -11117.36) * mm});
            skLineSegment(sketch, "E412", {"start": v(7689.24, -10731.21) * mm, "end": v(8425.63, -9994.83) * mm});
            skLineSegment(sketch, "E413", {"start": v(8425.63, -9797.26) * mm, "end": v(9162, -10533.65) * mm});
            skLineSegment(sketch, "E414", {"start": v(8425.63, -9994.83) * mm, "end": v(9162, -10731.21) * mm});
            skLineSegment(sketch, "E415", {"start": v(8349.3, -10062.18) * mm, "end": v(8255, -9967.89) * mm});
            skLineSegment(sketch, "E416", {"start": v(8255, -9967.89) * mm, "end": v(8425.63, -9797.26) * mm});
            skLineSegment(sketch, "E417", {"start": v(6744.86, -8116.5) * mm, "end": v(7141.45, -8513.09) * mm});
            skLineSegment(sketch, "E418", {"start": v(7028.85, -6464.58) * mm, "end": v(6348.27, -7145.17) * mm});
            skLineSegment(sketch, "E419", {"start": v(8425.63, -9797.26) * mm, "end": v(8371.74, -9743.38) * mm});
            skLineSegment(sketch, "E420", {"start": v(8371.74, -9743.38) * mm, "end": v(8308.88, -9806.24) * mm});
            skLineSegment(sketch, "E421", {"start": v(8308.88, -9806.24) * mm, "end": v(8362.76, -9860.13) * mm});
            skLineSegment(sketch, "E422", {"start": v(7141.45, -7938.35) * mm, "end": v(7086.1, -7883) * mm});
            skLineSegment(sketch, "E423", {"start": v(7086.1, -7883) * mm, "end": v(6798.74, -8170.38) * mm});
            skLineSegment(sketch, "E424", {"start": v(6348.27, -7145.17) * mm, "end": v(6403.6, -7200.51) * mm});
            skLineSegment(sketch, "E425", {"start": v(6403.6, -7200.51) * mm, "end": v(6116.24, -7487.88) * mm});
            skSolve(sketch);
        }
        {
            var Q0;
            Q0=makeQuery(id+"F12.imprint","IMPRINT",FACE,{"disambiguationData":[TD([[makeQuery(id+"F12.imprint","IMPRINT",EDGE,{"derivedFrom":sQuery(id+"F12.wireOp",EDGE,"E353")}),-1.0]])]});
            var Q1;
            Q1=makeQuery(id+"F12.imprint","IMPRINT",FACE,{"disambiguationData":[TD([[makeQuery(id+"F12.imprint","IMPRINT",EDGE,{"derivedFrom":sQuery(id+"F12.wireOp",EDGE,"E356")}),1.0]])]});
            var Q2;
            Q2=makeQuery(id+"F12.imprint","IMPRINT",FACE,{"disambiguationData":[TD([[makeQuery(id+"F12.imprint","IMPRINT",EDGE,{"derivedFrom":sQuery(id+"F12.wireOp",EDGE,"E361")}),-1.0]])]});
            extrude(context, id + "F13", {"entities" : qUnion([Q0, Q1, Q2]), "operationType" : NewBodyOperationType.ADD, "depth" : 2466.97 * mm, "offsetDistance" : 25.4 * mm});
        }
        {
            var Q0;
            Q0=makeQuery(id+"F12.imprint","IMPRINT",FACE,{"disambiguationData":[TD([[makeQuery(id+"F12.imprint","IMPRINT",EDGE,{"derivedFrom":sQuery(id+"F12.wireOp",EDGE,"E366")}),1.0]])]});
            var Q1;
            Q1=makeQuery(id+"F12.imprint","IMPRINT",FACE,{"disambiguationData":[TD([[makeQuery(id+"F12.imprint","IMPRINT",EDGE,{"derivedFrom":sQuery(id+"F12.wireOp",EDGE,"E365.bottom")}),-1.0]])]});
            var Q2;
            Q2=makeQuery(id+"F12.imprint","IMPRINT",FACE,{"disambiguationData":[TD([[makeQuery(id+"F12.imprint","IMPRINT",EDGE,{"derivedFrom":sQuery(id+"F12.wireOp",EDGE,"E363.bottom")}),1.0]])]});
            var Q3;
            Q3=makeQuery(id+"F12.imprint","IMPRINT",FACE,{"disambiguationData":[TD([[makeQuery(id+"F12.imprint","IMPRINT",EDGE,{"derivedFrom":sQuery(id+"F12.wireOp",EDGE,"E377")}),1.0]])]});
            var Q4;
            {var subQ0=sQuery(id+"F12.wireOp",EDGE,"FJR4ja9j-p2ak-Trk9-4ySA-Szw4HQpRkR0A");Q4=makeQuery(id+"F12.imprint","IMPRINT",FACE,{"disambiguationData":[TD([[makeQuery(id+"F12.imprint","IMPRINT",EDGE,{"derivedFrom":subQ0}),-1.0]])]});}
            var Q5;
            Q5=makeQuery(id+"F12.imprint","IMPRINT",FACE,{"disambiguationData":[TD([[makeQuery(id+"F12.imprint","IMPRINT",EDGE,{"derivedFrom":sQuery(id+"F12.wireOp",EDGE,"E405.bottom")}),1.0]])]});
            var Q6;
            Q6=makeQuery(id+"F12.imprint","IMPRINT",FACE,{"disambiguationData":[TD([[makeQuery(id+"F12.imprint","IMPRINT",EDGE,{"derivedFrom":sQuery(id+"F12.wireOp",EDGE,"E404.bottom")}),1.0]])]});
            var Q7;
            {var subQ3=sQuery(id+"F12.wireOp",EDGE,"E402");Q7=makeQuery(id+"F12.imprint","IMPRINT",FACE,{"disambiguationData":[TD([[makeQuery(id+"F12.imprint","IMPRINT",EDGE,{"derivedFrom":subQ3}),1.0]])]});}
            var Q8;
            Q8=makeQuery(id+"F12.imprint","IMPRINT",FACE,{"disambiguationData":[TD([[makeQuery(id+"F12.imprint","IMPRINT",EDGE,{"derivedFrom":sQuery(id+"F12.wireOp",EDGE,"E353")}),1.0]])]});
            var Q9;
            {var subQ4=sQuery(id+"F12.wireOp",EDGE,"jYt5KyJm-HCuG-WGCo-9pIC-Yxc8FQPq2GHh");Q9=makeQuery(id+"F12.imprint","IMPRINT",FACE,{"disambiguationData":[TD([[makeQuery(id+"F12.imprint","IMPRINT",EDGE,{"derivedFrom":subQ4}),-1.0]])]});}
            var Q10;
            {var subQ4=sQuery(id+"F12.wireOp",EDGE,"E411");Q10=makeQuery(id+"F12.imprint","IMPRINT",FACE,{"disambiguationData":[TD([[makeQuery(id+"F12.imprint","IMPRINT",EDGE,{"derivedFrom":subQ4}),-1.0]])]});}
            var Q11;
            {var subQ0=sQuery(id+"F12.wireOp",EDGE,"E389");Q11=makeQuery(id+"F12.imprint","IMPRINT",FACE,{"disambiguationData":[TD([[makeQuery(id+"F12.imprint","IMPRINT",EDGE,{"derivedFrom":subQ0}),-1.0]])]});}
            extrude(context, id + "F14", {"entities" : qUnion([Q0, Q1, Q2, Q3, Q4, Q5, Q6, Q7, Q8, Q9, Q10, Q11]), "depth" : 914.4 * mm, "offsetDistance" : 25.4 * mm});
        }
        {
            var Q0;
            {var subQ0=sQuery(id+"F12.wireOp",EDGE,"E410");Q0=makeQuery(id+"F12.imprint","IMPRINT",FACE,{"disambiguationData":[TD([[makeQuery(id+"F12.imprint","IMPRINT",EDGE,{"derivedFrom":subQ0}),1.0]])]});}
            extrude(context, id + "F15", {"entities" : qUnion([Q0]), "depth" : 762 * mm, "offsetDistance" : 25.4 * mm});
        }
        {
            var Q0;
            {var subQ0=sQuery(id+"F12.wireOp",EDGE,"E392");Q0=makeQuery(id+"F12.imprint","IMPRINT",FACE,{"disambiguationData":[TD([[makeQuery(id+"F12.imprint","IMPRINT",EDGE,{"derivedFrom":subQ0}),-1.0]])]});}
            extrude(context, id + "F16", {"entities" : qUnion([Q0]), "depth" : 609.6 * mm, "offsetDistance" : 25.4 * mm});
        }
        {
            var Q0;
            Q0=qCreatedBy(makeId("Top.planeOp"),FACE);
            var sketch = newSketch(context, id + "F17", { "sketchPlane" : qUnion([Q0])});
            skLineSegment(sketch, "E426", {"start": v(6229.38, -12191.07) * mm, "end": v(12470.66, -18432.35) * mm});
            skLineSegment(sketch, "E427", {"start": v(12470.66, -18432.35) * mm, "end": v(18074.34, -12828.67) * mm});
            skLineSegment(sketch, "E428", {"start": v(18074.34, -12828.67) * mm, "end": v(12470.66, -7225) * mm});
            skLineSegment(sketch, "E429", {"start": v(12470.66, -7422.56) * mm, "end": v(17876.78, -12828.67) * mm});
            skLineSegment(sketch, "E430", {"start": v(17876.78, -12828.67) * mm, "end": v(12470.66, -18234.78) * mm});
            skLineSegment(sketch, "E431", {"start": v(6121.62, -12298.84) * mm, "end": v(6229.38, -12191.07) * mm});
            skLineSegment(sketch, "E432.trimOffspring", {"start": v(12470.66, -18234.78) * mm, "end": v(6328.17, -12092.29) * mm});
            skLineSegment(sketch, "E433", {"start": v(6328.17, -12092.29) * mm, "end": v(6229.38, -12191.07) * mm});
            skLineSegment(sketch, "E434", {"start": v(12470.66, -7422.56) * mm, "end": v(12416.78, -7476.44) * mm});
            skLineSegment(sketch, "E435", {"start": v(10614.9, -9278.32) * mm, "end": v(10516.11, -9179.54) * mm});
            skLineSegment(sketch, "E436", {"start": v(10516.11, -9179.54) * mm, "end": v(11635.5, -8060.15) * mm});
            skLineSegment(sketch, "E437.bottom", {"start": v(12548.5, -9535.91) * mm, "end": v(16535.72, -13523.14) * mm});
            skLineSegment(sketch, "E437.top", {"start": v(11111.65, -10972.75) * mm, "end": v(15098.88, -14959.98) * mm});
            skLineSegment(sketch, "E437.left", {"start": v(12548.5, -9535.91) * mm, "end": v(11111.65, -10972.75) * mm});
            skLineSegment(sketch, "E437.right", {"start": v(16535.72, -13523.14) * mm, "end": v(15098.88, -14959.98) * mm});
            skLineSegment(sketch, "E438.bottom", {"start": v(11099.68, -12134.2) * mm, "end": v(14512.17, -15546.7) * mm});
            skLineSegment(sketch, "E438.top", {"start": v(9752.64, -13481.24) * mm, "end": v(13165.13, -16893.73) * mm});
            skLineSegment(sketch, "E438.left", {"start": v(11099.68, -12134.2) * mm, "end": v(9752.64, -13481.24) * mm});
            skLineSegment(sketch, "E438.right", {"start": v(14512.17, -15546.7) * mm, "end": v(13165.13, -16893.73) * mm});
            skLineSegment(sketch, "E439", {"start": v(14207.57, -10021.57) * mm, "end": v(17445.72, -13259.72) * mm, "construction": true});
            skLineSegment(sketch, "E440", {"start": v(9035.2, -13937.22) * mm, "end": v(12901.71, -17803.73) * mm, "construction": true});
            skLineSegment(sketch, "E441", {"start": v(13165.13, -16893.73) * mm, "end": v(12578.42, -17480.44) * mm, "construction": true});
            skLineSegment(sketch, "E442", {"start": v(15098.88, -14959.98) * mm, "end": v(14512.17, -15546.7) * mm, "construction": true});
            skLineSegment(sketch, "E443", {"start": v(16535.72, -13523.14) * mm, "end": v(17122.43, -12936.43) * mm, "construction": true});
            skLineSegment(sketch, "E444", {"start": v(12318, -7377.66) * mm, "end": v(12416.78, -7476.44) * mm});
            skLineSegment(sketch, "E445", {"start": v(11635.5, -8060.15) * mm, "end": v(11734.28, -8158.94) * mm});
            skLineSegment(sketch, "E446.trimOffspring", {"start": v(12318, -7377.66) * mm, "end": v(12470.66, -7225) * mm});
            skLineSegment(sketch, "E447.trimOffspring", {"start": v(11734.28, -8158.94) * mm, "end": v(10614.9, -9278.32) * mm});
            skLineSegment(sketch, "E448.bottom", {"start": v(6435.93, -12056.37) * mm, "end": v(6974.74, -11517.55) * mm});
            skLineSegment(sketch, "E448.top", {"start": v(6974.74, -12595.18) * mm, "end": v(7513.56, -12056.37) * mm});
            skLineSegment(sketch, "E448.left", {"start": v(6435.93, -12056.37) * mm, "end": v(6974.74, -12595.18) * mm});
            skLineSegment(sketch, "E448.right", {"start": v(6974.74, -11517.55) * mm, "end": v(7513.56, -12056.37) * mm});
            skLineSegment(sketch, "E449.bottom", {"start": v(7046.59, -11445.71) * mm, "end": v(7585.4, -10906.9) * mm});
            skLineSegment(sketch, "E449.top", {"start": v(7585.4, -11984.53) * mm, "end": v(8124.22, -11445.71) * mm});
            skLineSegment(sketch, "E449.left", {"start": v(7046.59, -11445.71) * mm, "end": v(7585.4, -11984.53) * mm});
            skLineSegment(sketch, "E449.right", {"start": v(7585.4, -10906.9) * mm, "end": v(8124.22, -11445.71) * mm});
            skSolve(sketch);
        }
        {
            var Q0;
            Q0=makeQuery(id+"F17.imprint","IMPRINT",FACE,{"disambiguationData":[TD([[makeQuery(id+"F17.imprint","IMPRINT",EDGE,{"derivedFrom":sQuery(id+"F17.wireOp",EDGE,"E426")}),1.0]])]});
            var Q1;
            Q1=makeQuery(id+"F17.imprint","IMPRINT",FACE,{"disambiguationData":[TD([[makeQuery(id+"F17.imprint","IMPRINT",EDGE,{"derivedFrom":sQuery(id+"F17.wireOp",EDGE,"E435")}),-1.0]])]});
            extrude(context, id + "F18", {"entities" : qUnion([Q0, Q1]), "operationType" : NewBodyOperationType.ADD, "depth" : 2466.97 * mm, "offsetDistance" : 25.4 * mm});
        }
        {
            var Q0;
            Q0=makeQuery(id+"F17.imprint","IMPRINT",FACE,{"disambiguationData":[TD([[makeQuery(id+"F17.imprint","IMPRINT",EDGE,{"derivedFrom":sQuery(id+"F17.wireOp",EDGE,"E438.bottom")}),-1.0]])]});
            var Q1;
            Q1=makeQuery(id+"F17.imprint","IMPRINT",FACE,{"disambiguationData":[TD([[makeQuery(id+"F17.imprint","IMPRINT",EDGE,{"derivedFrom":sQuery(id+"F17.wireOp",EDGE,"E437.bottom")}),-1.0]])]});
            var Q2;
            Q2=makeQuery(id+"F17.imprint","IMPRINT",FACE,{"disambiguationData":[TD([[makeQuery(id+"F17.imprint","IMPRINT",EDGE,{"derivedFrom":sQuery(id+"F17.wireOp",EDGE,"E449.bottom")}),-1.0]])]});
            var Q3;
            Q3=makeQuery(id+"F17.imprint","IMPRINT",FACE,{"disambiguationData":[TD([[makeQuery(id+"F17.imprint","IMPRINT",EDGE,{"derivedFrom":sQuery(id+"F17.wireOp",EDGE,"E448.bottom")}),-1.0]])]});
            extrude(context, id + "F19", {"entities" : qUnion([Q0, Q1, Q2, Q3]), "depth" : 1676.4 * mm, "offsetDistance" : 25.4 * mm});
        }
    });
